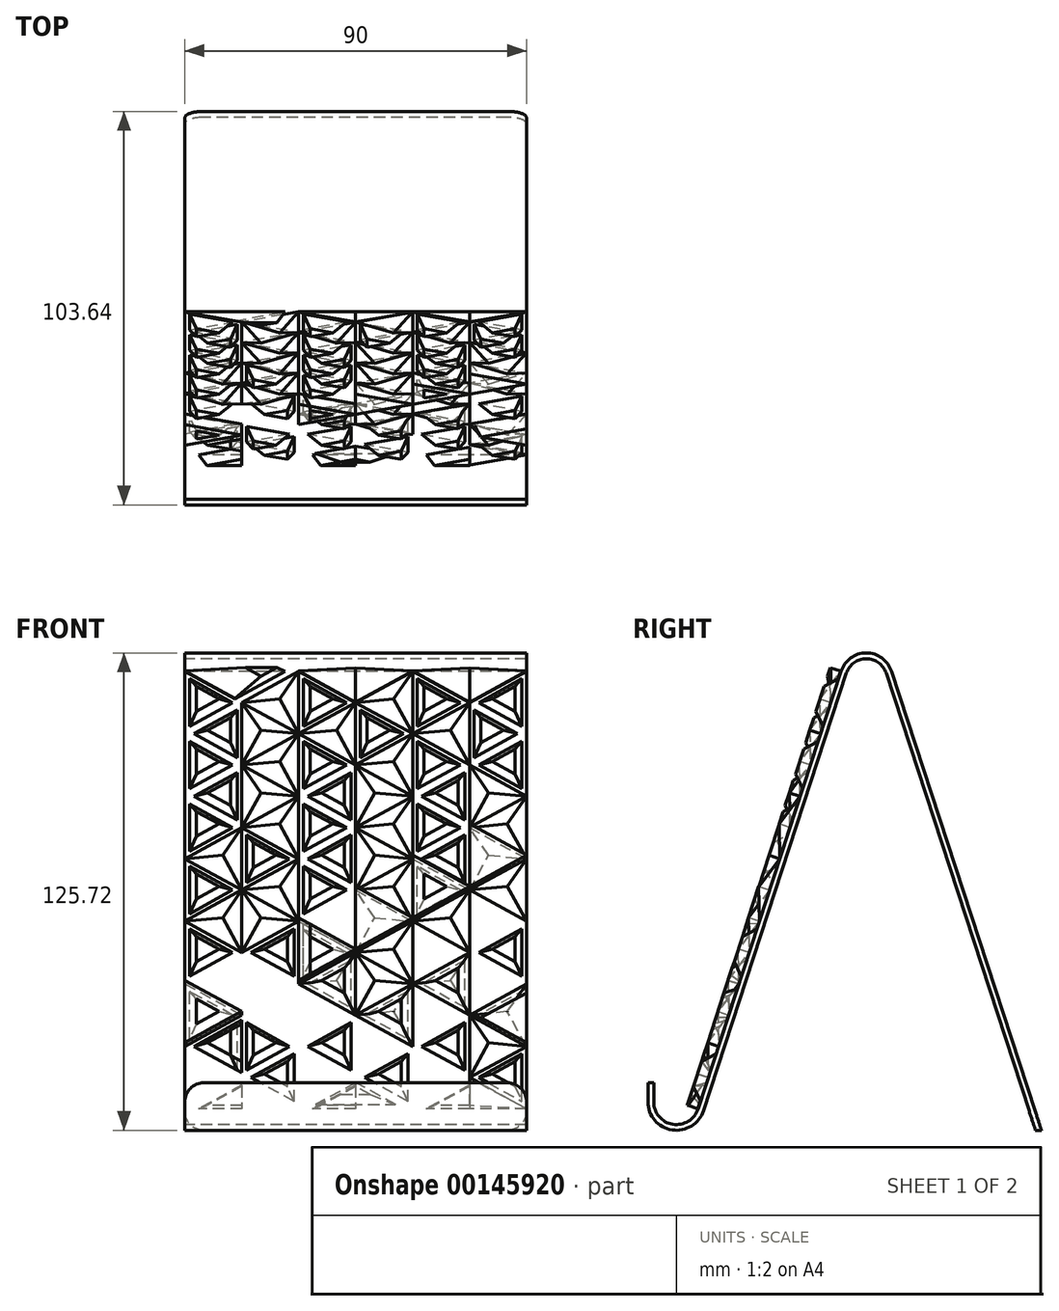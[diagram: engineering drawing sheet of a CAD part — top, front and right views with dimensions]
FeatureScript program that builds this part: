
annotation { "Feature Type Name" : "Feature", "Feature Type Description" : "" }
export const myFeature = defineFeature(function(context is Context, id is Id, definition is map)
    precondition{}
    {
        {
            var Q0;
            Q0=qCreatedBy(makeId("Right.planeOp"),FACE);
            var sketch = newSketch(context, id + "F0", { "sketchPlane" : qUnion([Q0])});
            skArc(sketch, "E0", {"start": v(-7.5, 0) * mm, "mid": v(-1.18, -7.4) * mm, "end": v(7.13, -2.33) * mm});
            skArc(sketch, "E1", {"start": v(55.23, 112.93) * mm, "mid": v(50, 116.72) * mm, "end": v(44.77, 112.93) * mm});
            skLineSegment(sketch, "E2", {"start": v(44.77, 112.93) * mm, "end": v(7.13, -2.33) * mm});
            skLineSegment(sketch, "E3", {"start": v(50, 111.22) * mm, "end": v(50, 0) * mm, "construction": true});
            skLineSegment(sketch, "E4.MirrorCS", {"start": v(55.23, 112.93) * mm, "end": v(94.56, -7.5) * mm});
            skLineSegment(sketch, "E5", {"start": v(0, -7.5) * mm, "end": v(108.37, -7.5) * mm, "construction": true});
            skLineSegment(sketch, "E6", {"start": v(-7.5, 0) * mm, "end": v(-7.5, 5) * mm});
            skLineSegment(sketch, "E7.0", {"start": v(-6, 0) * mm, "end": v(-6, 5) * mm});
            skLineSegment(sketch, "E7.1", {"start": v(56.65, 113.4) * mm, "end": v(96.14, -7.5) * mm});
            skArc(sketch, "E7.2", {"start": v(56.65, 113.4) * mm, "mid": v(50, 118.22) * mm, "end": v(43.35, 113.4) * mm});
            skLineSegment(sketch, "E7.3", {"start": v(43.35, 113.4) * mm, "end": v(5.7, -1.86) * mm});
            skArc(sketch, "E7.4", {"start": v(-6, 0) * mm, "mid": v(-0.94, -5.93) * mm, "end": v(5.7, -1.86) * mm});
            skLineSegment(sketch, "E8", {"start": v(94.56, -7.5) * mm, "end": v(96.14, -7.5) * mm});
            skLineSegment(sketch, "E9", {"start": v(-7.5, 5) * mm, "end": v(-6, 5) * mm});
            skSolve(sketch);
        }
        {
            var Q0;
            Q0=makeQuery(id+"F0.imprint","IMPRINT",FACE,{"disambiguationData":[TD([[makeQuery(id+"F0.imprint","IMPRINT",EDGE,{"derivedFrom":sQuery(id+"F0.wireOp",EDGE,"E0")}),1.0]])]});
            extrude(context, id + "F1", {"entities" : qUnion([Q0]), "depth" : 90 * mm, "symmetric" : true});
        }
        {
            var Q0;
            Q0=makeQuery(id+"F1.opExtrude","CAP_EDGE",EDGE,{"disambiguationData":[OSD([sQuery(id+"F0.wireOp",EDGE,"E9")])],"isStart":false});
            var Q1;
            Q1=makeQuery(id+"F1.opExtrude","CAP_EDGE",EDGE,{"disambiguationData":[OSD([sQuery(id+"F0.wireOp",EDGE,"E9")])],"isStart":true});
            var Q2;
            Q2=makeQuery(id+"F1.opExtrude","CAP_EDGE",EDGE,{"disambiguationData":[OSD([sQuery(id+"F0.wireOp",EDGE,"E8")])],"isStart":true});
            var Q3;
            Q3=makeQuery(id+"F1.opExtrude","CAP_EDGE",EDGE,{"disambiguationData":[OSD([sQuery(id+"F0.wireOp",EDGE,"E8")])],"isStart":false});
            fillet(context, id + "F2", {"entities" : qUnion([Q0, Q1, Q2, Q3]), "radius" : 5 * mm, "tangentPropagation" : true, "allowEdgeOverflow" : false});
        }
        {
            var Q0;
            Q0=makeQuery(id+"F1.opExtrude","SWEPT_FACE",FACE,{"disambiguationData":[OSD([sQuery(id+"F0.wireOp",EDGE,"E7.3")])]});
            var sketch = newSketch(context, id + "F3", { "sketchPlane" : qUnion([Q0])});
            skLineSegment(sketch, "E10", {"start": v(-45, 121.25) * mm, "end": v(45, 121.25) * mm});
            skLineSegment(sketch, "E11", {"start": v(45, 121.25) * mm, "end": v(45, 0) * mm});
            skLineSegment(sketch, "E12", {"start": v(45, 0) * mm, "end": v(-45, 0) * mm});
            skLineSegment(sketch, "E13", {"start": v(-45, 0) * mm, "end": v(-45, 121.25) * mm});
            skPoint(sketch, "E14", {"position": v(-45, 121.25) * mm});
            skPoint(sketch, "E15", {"position": v(45, 121.25) * mm});
            skPoint(sketch, "E16", {"position": v(45, 0) * mm});
            skPoint(sketch, "E17", {"position": v(-45, 0) * mm});
            skPoint(sketch, "E18", {"position": v(-15, 121.25) * mm});
            skPoint(sketch, "E19", {"position": v(15, 121.25) * mm});
            skLineSegment(sketch, "E20", {"start": v(-15, 121.25) * mm, "end": v(-15, 0) * mm});
            skLineSegment(sketch, "E21", {"start": v(15, 121.25) * mm, "end": v(15, 0) * mm});
            skPoint(sketch, "E22", {"position": v(-45, 103.93) * mm});
            skPoint(sketch, "E23", {"position": v(-45, 86.6) * mm});
            skPoint(sketch, "E24", {"position": v(-45, 69.28) * mm});
            skPoint(sketch, "E25", {"position": v(-45, 51.96) * mm});
            skPoint(sketch, "E26", {"position": v(-45, 34.64) * mm});
            skPoint(sketch, "E27", {"position": v(-45, 17.32) * mm});
            skLineSegment(sketch, "E28", {"start": v(-15, 103.93) * mm, "end": v(15, 121.25) * mm});
            skLineSegment(sketch, "E29", {"start": v(-15, 121.25) * mm, "end": v(-45, 103.93) * mm});
            skLineSegment(sketch, "E30", {"start": v(-45, 121.25) * mm, "end": v(45, 69.28) * mm});
            skLineSegment(sketch, "E31", {"start": v(-15, 103.93) * mm, "end": v(-45, 86.6) * mm});
            skLineSegment(sketch, "E32", {"start": v(-45, 103.93) * mm, "end": v(45, 51.96) * mm});
            skLineSegment(sketch, "E33", {"start": v(-45, 69.28) * mm, "end": v(45, 121.25) * mm});
            skLineSegment(sketch, "E34", {"start": v(-45, 51.96) * mm, "end": v(45, 103.93) * mm});
            skLineSegment(sketch, "E35", {"start": v(-15, 121.25) * mm, "end": v(45, 86.6) * mm});
            skLineSegment(sketch, "E36", {"start": v(15, 121.25) * mm, "end": v(45, 103.93) * mm});
            skLineSegment(sketch, "E37", {"start": v(-45, 86.6) * mm, "end": v(45, 34.64) * mm});
            skLineSegment(sketch, "E38", {"start": v(-45, 69.28) * mm, "end": v(-15, 51.96) * mm});
            skLineSegment(sketch, "E39", {"start": v(45, 86.6) * mm, "end": v(-15, 51.96) * mm});
            skLineSegment(sketch, "E40", {"start": v(45, 69.28) * mm, "end": v(-45, 17.32) * mm});
            skLineSegment(sketch, "E41", {"start": v(-45, 0) * mm, "end": v(45, 51.96) * mm});
            skLineSegment(sketch, "E42", {"start": v(-45, 34.64) * mm, "end": v(-15, 51.96) * mm});
            skLineSegment(sketch, "E43", {"start": v(-45, 51.96) * mm, "end": v(-15, 34.64) * mm});
            skLineSegment(sketch, "E44", {"start": v(-45, 34.64) * mm, "end": v(15, 0) * mm});
            skLineSegment(sketch, "E45", {"start": v(15, 17.32) * mm, "end": v(15, 17.32) * mm});
            skLineSegment(sketch, "E46", {"start": v(-45, 17.32) * mm, "end": v(-15, 0) * mm});
            skLineSegment(sketch, "E47", {"start": v(-15, 51.96) * mm, "end": v(45, 17.32) * mm});
            skLineSegment(sketch, "E48", {"start": v(-15, 0) * mm, "end": v(15, 17.32) * mm});
            skLineSegment(sketch, "E49", {"start": v(-15, 34.64) * mm, "end": v(-15, 34.64) * mm});
            skLineSegment(sketch, "E50", {"start": v(45, 0) * mm, "end": v(-15, 34.64) * mm});
            skLineSegment(sketch, "E51", {"start": v(15, 17.32) * mm, "end": v(45, 34.64) * mm});
            skLineSegment(sketch, "E52", {"start": v(15, 0) * mm, "end": v(45, 17.32) * mm});
            skPoint(sketch, "E53", {"position": v(0, 112.59) * mm});
            skLineSegment(sketch, "E54", {"start": v(0, 121.25) * mm, "end": v(0, 0) * mm});
            skPoint(sketch, "E55", {"position": v(-30, 112.59) * mm});
            skLineSegment(sketch, "E56", {"start": v(-30, 121.25) * mm, "end": v(-30, 0) * mm});
            skPoint(sketch, "E56.endSnap0", {"position": v(-30, 8.66) * mm});
            skPoint(sketch, "E57", {"position": v(30, 112.59) * mm});
            skLineSegment(sketch, "E58", {"start": v(30, 121.25) * mm, "end": v(30, 0) * mm});
            skPoint(sketch, "E58.endSnap0", {"position": v(30, 25.98) * mm});
            skPoint(sketch, "E59", {"position": v(-30, 95.27) * mm});
            skPoint(sketch, "E60", {"position": v(-30, 77.94) * mm});
            skPoint(sketch, "E61", {"position": v(-30, 60.62) * mm});
            skPoint(sketch, "E62", {"position": v(-30, 43.3) * mm});
            skPoint(sketch, "E63", {"position": v(-30, 25.98) * mm});
            skPoint(sketch, "E64", {"position": v(-30, 0) * mm});
            skPoint(sketch, "E65", {"position": v(-15, 17.32) * mm});
            skPoint(sketch, "E66", {"position": v(-15, 34.64) * mm});
            skPoint(sketch, "E67", {"position": v(-15, 51.96) * mm});
            skPoint(sketch, "E68", {"position": v(-15, 69.28) * mm});
            skPoint(sketch, "E69", {"position": v(-15, 86.6) * mm});
            skPoint(sketch, "E70", {"position": v(0, 8.66) * mm});
            skPoint(sketch, "E71", {"position": v(0, 25.98) * mm});
            skPoint(sketch, "E72", {"position": v(0, 43.3) * mm});
            skPoint(sketch, "E73", {"position": v(0, 60.62) * mm});
            skPoint(sketch, "E74", {"position": v(15, 103.93) * mm});
            skPoint(sketch, "E75", {"position": v(0, 95.27) * mm});
            skPoint(sketch, "E76", {"position": v(0, 77.94) * mm});
            skPoint(sketch, "E77", {"position": v(15, 69.28) * mm});
            skPoint(sketch, "E78", {"position": v(15, 86.6) * mm});
            skPoint(sketch, "E79", {"position": v(15, 51.96) * mm});
            skPoint(sketch, "E80", {"position": v(15, 34.64) * mm});
            skPoint(sketch, "E81", {"position": v(15, 17.32) * mm});
            skPoint(sketch, "E82", {"position": v(15, 0) * mm});
            skPoint(sketch, "E83", {"position": v(30, 8.66) * mm});
            skPoint(sketch, "E84", {"position": v(30, 43.3) * mm});
            skPoint(sketch, "E85", {"position": v(30, 60.62) * mm});
            skPoint(sketch, "E86", {"position": v(30, 77.94) * mm});
            skPoint(sketch, "E87", {"position": v(30, 95.27) * mm});
            skPoint(sketch, "E88", {"position": v(45, 103.93) * mm});
            skSolve(sketch);
        }
        {
            var Q0;
            {var subQ0=sQuery(id+"F3.wireOp",EDGE,"E30");var subQ1=sQuery(id+"F3.wireOp",EDGE,"E13");var subQ2=makeQuery(id+"F3.imprint","INTERSECT",VERTEX,{"derivedFrom":[sQuery(id+"F3.wireOp",EDGE,"E10"),subQ1,subQ0]});Q0=makeQuery(id+"F3.imprint","IMPRINT",FACE,{"disambiguationData":[TD([[makeQuery(id+"F3.imprint","IMPRINT",EDGE,{"disambiguationData":[TD([[subQ2,-1.0]])],"derivedFrom":subQ1}),1.0]])]});}
            var Q1;
            {var subQ0=sQuery(id+"F3.wireOp",EDGE,"E29");var subQ3=sQuery(id+"F3.wireOp",EDGE,"E30");var subQ5=makeQuery(id+"F3.imprint","INTERSECT",VERTEX,{"derivedFrom":[subQ0,subQ3,sQuery(id+"F3.wireOp",EDGE,"E56")]});Q1=makeQuery(id+"F3.imprint","IMPRINT",FACE,{"disambiguationData":[TD([[makeQuery(id+"F3.imprint","IMPRINT",EDGE,{"disambiguationData":[TD([[subQ5,1.0]])],"derivedFrom":subQ0}),1.0]])]});}
            var Q2;
            {var subQ0=sQuery(id+"F3.wireOp",EDGE,"E32");var subQ1=sQuery(id+"F3.wireOp",EDGE,"E13");var subQ2=makeQuery(id+"F3.imprint","INTERSECT",VERTEX,{"derivedFrom":[subQ1,sQuery(id+"F3.wireOp",EDGE,"E29"),subQ0]});Q2=makeQuery(id+"F3.imprint","IMPRINT",FACE,{"disambiguationData":[TD([[makeQuery(id+"F3.imprint","IMPRINT",EDGE,{"disambiguationData":[TD([[subQ2,-1.0]])],"derivedFrom":subQ1}),1.0]])]});}
            var Q3;
            {var subQ1=sQuery(id+"F3.wireOp",EDGE,"E20");var subQ3=sQuery(id+"F3.wireOp",EDGE,"E32");var subQ4=makeQuery(id+"F3.imprint","INTERSECT",VERTEX,{"derivedFrom":[subQ1,subQ3,sQuery(id+"F3.wireOp",EDGE,"E33")]});Q3=makeQuery(id+"F3.imprint","IMPRINT",FACE,{"disambiguationData":[TD([[makeQuery(id+"F3.imprint","IMPRINT",EDGE,{"disambiguationData":[TD([[subQ4,1.0]])],"derivedFrom":subQ3}),1.0]])]});}
            var Q4;
            {var subQ0=sQuery(id+"F3.wireOp",EDGE,"E37");var subQ1=sQuery(id+"F3.wireOp",EDGE,"E13");var subQ2=makeQuery(id+"F3.imprint","INTERSECT",VERTEX,{"derivedFrom":[subQ1,sQuery(id+"F3.wireOp",EDGE,"E31"),subQ0]});Q4=makeQuery(id+"F3.imprint","IMPRINT",FACE,{"disambiguationData":[TD([[makeQuery(id+"F3.imprint","IMPRINT",EDGE,{"disambiguationData":[TD([[subQ2,-1.0]])],"derivedFrom":subQ1}),1.0]])]});}
            var Q5;
            {var subQ0=sQuery(id+"F3.wireOp",EDGE,"E33");var subQ1=sQuery(id+"F3.wireOp",EDGE,"E20");var subQ2=makeQuery(id+"F3.imprint","INTERSECT",VERTEX,{"derivedFrom":[subQ1,sQuery(id+"F3.wireOp",EDGE,"E32"),subQ0]});Q5=makeQuery(id+"F3.imprint","IMPRINT",FACE,{"disambiguationData":[TD([[makeQuery(id+"F3.imprint","IMPRINT",EDGE,{"disambiguationData":[TD([[subQ2,-1.0]])],"derivedFrom":subQ1}),-1.0]])]});}
            var Q6;
            {var subQ0=sQuery(id+"F3.wireOp",EDGE,"E38");var subQ1=sQuery(id+"F3.wireOp",EDGE,"E13");var subQ2=makeQuery(id+"F3.imprint","INTERSECT",VERTEX,{"derivedFrom":[subQ1,sQuery(id+"F3.wireOp",EDGE,"E33"),subQ0]});Q6=makeQuery(id+"F3.imprint","IMPRINT",FACE,{"disambiguationData":[TD([[makeQuery(id+"F3.imprint","IMPRINT",EDGE,{"disambiguationData":[TD([[subQ2,-1.0]])],"derivedFrom":subQ1}),1.0]])]});}
            var Q7;
            {var subQ1=sQuery(id+"F3.wireOp",EDGE,"E20");var subQ3=sQuery(id+"F3.wireOp",EDGE,"E34");var subQ4=makeQuery(id+"F3.imprint","INTERSECT",VERTEX,{"derivedFrom":[subQ1,subQ3,sQuery(id+"F3.wireOp",EDGE,"E37")]});Q7=makeQuery(id+"F3.imprint","IMPRINT",FACE,{"disambiguationData":[TD([[makeQuery(id+"F3.imprint","IMPRINT",EDGE,{"disambiguationData":[TD([[subQ4,1.0]])],"derivedFrom":subQ3}),-1.0]])]});}
            var Q8;
            {var subQ0=sQuery(id+"F3.wireOp",EDGE,"E43");var subQ1=sQuery(id+"F3.wireOp",EDGE,"E13");var subQ2=makeQuery(id+"F3.imprint","INTERSECT",VERTEX,{"derivedFrom":[subQ1,sQuery(id+"F3.wireOp",EDGE,"E34"),subQ0]});Q8=makeQuery(id+"F3.imprint","IMPRINT",FACE,{"disambiguationData":[TD([[makeQuery(id+"F3.imprint","IMPRINT",EDGE,{"disambiguationData":[TD([[subQ2,-1.0]])],"derivedFrom":subQ1}),1.0]])]});}
            var Q9;
            {var subQ0=sQuery(id+"F3.wireOp",EDGE,"E42");var subQ3=sQuery(id+"F3.wireOp",EDGE,"E43");var subQ5=makeQuery(id+"F3.imprint","INTERSECT",VERTEX,{"derivedFrom":[subQ0,subQ3,sQuery(id+"F3.wireOp",EDGE,"E56")]});Q9=makeQuery(id+"F3.imprint","IMPRINT",FACE,{"disambiguationData":[TD([[makeQuery(id+"F3.imprint","IMPRINT",EDGE,{"disambiguationData":[TD([[subQ5,-1.0]])],"derivedFrom":subQ3}),1.0]])]});}
            var Q10;
            {var subQ0=sQuery(id+"F3.wireOp",EDGE,"E40");var subQ3=sQuery(id+"F3.wireOp",EDGE,"E44");var subQ5=makeQuery(id+"F3.imprint","INTERSECT",VERTEX,{"derivedFrom":[subQ0,subQ3]});Q10=makeQuery(id+"F3.imprint","IMPRINT",FACE,{"disambiguationData":[TD([[makeQuery(id+"F3.imprint","IMPRINT",EDGE,{"disambiguationData":[TD([[subQ5,-1.0]])],"derivedFrom":subQ0}),-1.0]])]});}
            var Q11;
            {var subQ0=sQuery(id+"F3.wireOp",EDGE,"E49");var subQ1=sQuery(id+"F3.wireOp",EDGE,"E40");var subQ2=makeQuery(id+"F3.imprint","INTERSECT",VERTEX,{"derivedFrom":[subQ1,subQ0]});Q11=makeQuery(id+"F3.imprint","IMPRINT",FACE,{"disambiguationData":[TD([[makeQuery(id+"F3.imprint","IMPRINT",EDGE,{"disambiguationData":[TD([[subQ2,-1.0]])],"derivedFrom":subQ1}),1.0]])]});}
            var Q12;
            {var subQ0=sQuery(id+"F3.wireOp",EDGE,"E41");var subQ5=sQuery(id+"F3.wireOp",EDGE,"E56");var subQ6=makeQuery(id+"F3.imprint","INTERSECT",VERTEX,{"derivedFrom":[subQ0,subQ5]});Q12=makeQuery(id+"F3.imprint","IMPRINT",FACE,{"disambiguationData":[TD([[makeQuery(id+"F3.imprint","IMPRINT",EDGE,{"disambiguationData":[TD([[subQ6,1.0]])],"derivedFrom":subQ5}),-1.0]])]});}
            var Q13;
            {var subQ0=sQuery(id+"F3.wireOp",EDGE,"E46");var subQ3=sQuery(id+"F3.wireOp",EDGE,"E41");var subQ5=makeQuery(id+"F3.imprint","INTERSECT",VERTEX,{"derivedFrom":[subQ3,subQ0]});Q13=makeQuery(id+"F3.imprint","IMPRINT",FACE,{"disambiguationData":[TD([[makeQuery(id+"F3.imprint","IMPRINT",EDGE,{"disambiguationData":[TD([[subQ5,-1.0]])],"derivedFrom":subQ3}),-1.0]])]});}
            var Q14;
            {var subQ1=sQuery(id+"F3.wireOp",EDGE,"E10");var subQ3=sQuery(id+"F3.wireOp",EDGE,"E54");var subQ4=makeQuery(id+"F3.imprint","INTERSECT",VERTEX,{"derivedFrom":[subQ1,subQ3]});Q14=makeQuery(id+"F3.imprint","IMPRINT",FACE,{"disambiguationData":[TD([[makeQuery(id+"F3.imprint","IMPRINT",EDGE,{"disambiguationData":[TD([[subQ4,-1.0]])],"derivedFrom":subQ3}),-1.0]])]});}
            var Q15;
            {var subQ1=sQuery(id+"F3.wireOp",EDGE,"E28");var subQ3=sQuery(id+"F3.wireOp",EDGE,"E54");var subQ4=makeQuery(id+"F3.imprint","INTERSECT",VERTEX,{"derivedFrom":[subQ1,sQuery(id+"F3.wireOp",EDGE,"E35"),subQ3]});Q15=makeQuery(id+"F3.imprint","IMPRINT",FACE,{"disambiguationData":[TD([[makeQuery(id+"F3.imprint","IMPRINT",EDGE,{"disambiguationData":[TD([[subQ4,-1.0]])],"derivedFrom":subQ3}),-1.0]])]});}
            var Q16;
            {var subQ0=sQuery(id+"F3.wireOp",EDGE,"E33");var subQ1=sQuery(id+"F3.wireOp",EDGE,"E32");var subQ2=makeQuery(id+"F3.imprint","INTERSECT",VERTEX,{"derivedFrom":[sQuery(id+"F3.wireOp",EDGE,"E20"),subQ1,subQ0]});Q16=makeQuery(id+"F3.imprint","IMPRINT",FACE,{"disambiguationData":[TD([[makeQuery(id+"F3.imprint","IMPRINT",EDGE,{"disambiguationData":[TD([[subQ2,-1.0]])],"derivedFrom":subQ1}),1.0]])]});}
            var Q17;
            {var subQ0=sQuery(id+"F3.wireOp",EDGE,"E37");var subQ1=sQuery(id+"F3.wireOp",EDGE,"E34");var subQ2=makeQuery(id+"F3.imprint","INTERSECT",VERTEX,{"derivedFrom":[sQuery(id+"F3.wireOp",EDGE,"E20"),subQ1,subQ0]});Q17=makeQuery(id+"F3.imprint","IMPRINT",FACE,{"disambiguationData":[TD([[makeQuery(id+"F3.imprint","IMPRINT",EDGE,{"disambiguationData":[TD([[subQ2,-1.0]])],"derivedFrom":subQ1}),-1.0]])]});}
            var Q18;
            {var subQ3=sQuery(id+"F3.wireOp",EDGE,"E54");var subQ5=sQuery(id+"F3.wireOp",EDGE,"E40");var subQ6=makeQuery(id+"F3.imprint","INTERSECT",VERTEX,{"derivedFrom":[subQ5,subQ3]});Q18=makeQuery(id+"F3.imprint","IMPRINT",FACE,{"disambiguationData":[TD([[makeQuery(id+"F3.imprint","IMPRINT",EDGE,{"disambiguationData":[TD([[subQ6,-1.0]])],"derivedFrom":subQ5}),-1.0]])]});}
            var Q19;
            {var subQ1=sQuery(id+"F3.wireOp",EDGE,"E40");var subQ6=sQuery(id+"F3.wireOp",EDGE,"E47");var subQ7=makeQuery(id+"F3.imprint","INTERSECT",VERTEX,{"derivedFrom":[subQ1,subQ6]});Q19=makeQuery(id+"F3.imprint","IMPRINT",FACE,{"disambiguationData":[TD([[makeQuery(id+"F3.imprint","IMPRINT",EDGE,{"disambiguationData":[TD([[subQ7,-1.0]])],"derivedFrom":subQ6}),-1.0]])]});}
            var Q20;
            {var subQ0=sQuery(id+"F3.wireOp",EDGE,"E54");var subQ1=sQuery(id+"F3.wireOp",EDGE,"E41");var subQ2=makeQuery(id+"F3.imprint","INTERSECT",VERTEX,{"derivedFrom":[subQ1,subQ0]});Q20=makeQuery(id+"F3.imprint","IMPRINT",FACE,{"disambiguationData":[TD([[makeQuery(id+"F3.imprint","IMPRINT",EDGE,{"disambiguationData":[TD([[subQ2,-1.0]])],"derivedFrom":subQ0}),-1.0]])]});}
            var Q21;
            {var subQ1=sQuery(id+"F3.wireOp",EDGE,"E12");var subQ3=sQuery(id+"F3.wireOp",EDGE,"E54");var subQ4=makeQuery(id+"F3.imprint","INTERSECT",VERTEX,{"derivedFrom":[subQ1,subQ3]});Q21=makeQuery(id+"F3.imprint","IMPRINT",FACE,{"disambiguationData":[TD([[makeQuery(id+"F3.imprint","IMPRINT",EDGE,{"disambiguationData":[TD([[subQ4,1.0]])],"derivedFrom":subQ3}),-1.0]])]});}
            var Q22;
            {var subQ1=sQuery(id+"F3.wireOp",EDGE,"E12");var subQ3=sQuery(id+"F3.wireOp",EDGE,"E44");var subQ4=makeQuery(id+"F3.imprint","INTERSECT",VERTEX,{"derivedFrom":[subQ1,subQ3]});Q22=makeQuery(id+"F3.imprint","IMPRINT",FACE,{"disambiguationData":[TD([[makeQuery(id+"F3.imprint","IMPRINT",EDGE,{"disambiguationData":[TD([[subQ4,1.0]])],"derivedFrom":subQ3}),1.0]])]});}
            var Q23;
            {var subQ0=sQuery(id+"F3.wireOp",EDGE,"E50");var subQ1=sQuery(id+"F3.wireOp",EDGE,"E21");var subQ2=makeQuery(id+"F3.imprint","INTERSECT",VERTEX,{"derivedFrom":[subQ1,subQ0]});Q23=makeQuery(id+"F3.imprint","IMPRINT",FACE,{"disambiguationData":[TD([[makeQuery(id+"F3.imprint","IMPRINT",EDGE,{"disambiguationData":[TD([[subQ2,-1.0]])],"derivedFrom":subQ0}),-1.0]])]});}
            var Q24;
            {var subQ0=sQuery(id+"F3.wireOp",EDGE,"E40");var subQ5=sQuery(id+"F3.wireOp",EDGE,"E54");var subQ7=makeQuery(id+"F3.imprint","INTERSECT",VERTEX,{"derivedFrom":[subQ0,subQ5]});Q24=makeQuery(id+"F3.imprint","IMPRINT",FACE,{"disambiguationData":[TD([[makeQuery(id+"F3.imprint","IMPRINT",EDGE,{"disambiguationData":[TD([[subQ7,-1.0]])],"derivedFrom":subQ5}),1.0]])]});}
            var Q25;
            {var subQ0=sQuery(id+"F3.wireOp",EDGE,"E39");var subQ1=sQuery(id+"F3.wireOp",EDGE,"E21");var subQ2=makeQuery(id+"F3.imprint","INTERSECT",VERTEX,{"derivedFrom":[subQ1,sQuery(id+"F3.wireOp",EDGE,"E32"),subQ0]});Q25=makeQuery(id+"F3.imprint","IMPRINT",FACE,{"disambiguationData":[TD([[makeQuery(id+"F3.imprint","IMPRINT",EDGE,{"disambiguationData":[TD([[subQ2,-1.0]])],"derivedFrom":subQ1}),-1.0]])]});}
            var Q26;
            {var subQ0=sQuery(id+"F3.wireOp",EDGE,"E34");var subQ1=sQuery(id+"F3.wireOp",EDGE,"E21");var subQ2=makeQuery(id+"F3.imprint","INTERSECT",VERTEX,{"derivedFrom":[subQ1,sQuery(id+"F3.wireOp",EDGE,"E30"),subQ0]});Q26=makeQuery(id+"F3.imprint","IMPRINT",FACE,{"disambiguationData":[TD([[makeQuery(id+"F3.imprint","IMPRINT",EDGE,{"disambiguationData":[TD([[subQ2,-1.0]])],"derivedFrom":subQ1}),-1.0]])]});}
            var Q27;
            {var subQ0=sQuery(id+"F3.wireOp",EDGE,"E33");var subQ1=sQuery(id+"F3.wireOp",EDGE,"E21");var subQ2=makeQuery(id+"F3.imprint","INTERSECT",VERTEX,{"derivedFrom":[subQ1,subQ0,sQuery(id+"F3.wireOp",EDGE,"E35")]});Q27=makeQuery(id+"F3.imprint","IMPRINT",FACE,{"disambiguationData":[TD([[makeQuery(id+"F3.imprint","IMPRINT",EDGE,{"disambiguationData":[TD([[subQ2,-1.0]])],"derivedFrom":subQ1}),-1.0]])]});}
            var Q28;
            {var subQ1=sQuery(id+"F3.wireOp",EDGE,"E21");var subQ3=sQuery(id+"F3.wireOp",EDGE,"E35");var subQ4=makeQuery(id+"F3.imprint","INTERSECT",VERTEX,{"derivedFrom":[subQ1,sQuery(id+"F3.wireOp",EDGE,"E33"),subQ3]});Q28=makeQuery(id+"F3.imprint","IMPRINT",FACE,{"disambiguationData":[TD([[makeQuery(id+"F3.imprint","IMPRINT",EDGE,{"disambiguationData":[TD([[subQ4,1.0]])],"derivedFrom":subQ3}),1.0]])]});}
            var Q29;
            {var subQ1=sQuery(id+"F3.wireOp",EDGE,"E10");var subQ3=sQuery(id+"F3.wireOp",EDGE,"E58");var subQ4=makeQuery(id+"F3.imprint","INTERSECT",VERTEX,{"derivedFrom":[subQ1,subQ3]});Q29=makeQuery(id+"F3.imprint","IMPRINT",FACE,{"disambiguationData":[TD([[makeQuery(id+"F3.imprint","IMPRINT",EDGE,{"disambiguationData":[TD([[subQ4,-1.0]])],"derivedFrom":subQ3}),-1.0]])]});}
            var Q30;
            {var subQ0=sQuery(id+"F3.wireOp",EDGE,"E35");var subQ1=sQuery(id+"F3.wireOp",EDGE,"E33");var subQ2=makeQuery(id+"F3.imprint","INTERSECT",VERTEX,{"derivedFrom":[sQuery(id+"F3.wireOp",EDGE,"E21"),subQ1,subQ0]});Q30=makeQuery(id+"F3.imprint","IMPRINT",FACE,{"disambiguationData":[TD([[makeQuery(id+"F3.imprint","IMPRINT",EDGE,{"disambiguationData":[TD([[subQ2,-1.0]])],"derivedFrom":subQ1}),-1.0]])]});}
            var Q31;
            {var subQ0=sQuery(id+"F3.wireOp",EDGE,"E34");var subQ1=sQuery(id+"F3.wireOp",EDGE,"E30");var subQ2=makeQuery(id+"F3.imprint","INTERSECT",VERTEX,{"derivedFrom":[sQuery(id+"F3.wireOp",EDGE,"E21"),subQ1,subQ0]});Q31=makeQuery(id+"F3.imprint","IMPRINT",FACE,{"disambiguationData":[TD([[makeQuery(id+"F3.imprint","IMPRINT",EDGE,{"disambiguationData":[TD([[subQ2,-1.0]])],"derivedFrom":subQ1}),1.0]])]});}
            var Q32;
            {var subQ0=sQuery(id+"F3.wireOp",EDGE,"E39");var subQ1=sQuery(id+"F3.wireOp",EDGE,"E32");var subQ2=makeQuery(id+"F3.imprint","INTERSECT",VERTEX,{"derivedFrom":[sQuery(id+"F3.wireOp",EDGE,"E21"),subQ1,subQ0]});Q32=makeQuery(id+"F3.imprint","IMPRINT",FACE,{"disambiguationData":[TD([[makeQuery(id+"F3.imprint","IMPRINT",EDGE,{"disambiguationData":[TD([[subQ2,-1.0]])],"derivedFrom":subQ1}),1.0]])]});}
            var Q33;
            {var subQ0=sQuery(id+"F3.wireOp",EDGE,"E58");var subQ1=sQuery(id+"F3.wireOp",EDGE,"E37");var subQ2=makeQuery(id+"F3.imprint","INTERSECT",VERTEX,{"derivedFrom":[subQ1,subQ0]});Q33=makeQuery(id+"F3.imprint","IMPRINT",FACE,{"disambiguationData":[TD([[makeQuery(id+"F3.imprint","IMPRINT",EDGE,{"disambiguationData":[TD([[subQ2,1.0]])],"derivedFrom":subQ1}),1.0]])]});}
            var Q34;
            {var subQ0=sQuery(id+"F3.wireOp",EDGE,"E58");var subQ1=sQuery(id+"F3.wireOp",EDGE,"E41");var subQ2=makeQuery(id+"F3.imprint","INTERSECT",VERTEX,{"derivedFrom":[subQ1,subQ0]});Q34=makeQuery(id+"F3.imprint","IMPRINT",FACE,{"disambiguationData":[TD([[makeQuery(id+"F3.imprint","IMPRINT",EDGE,{"disambiguationData":[TD([[subQ2,-1.0]])],"derivedFrom":subQ0}),-1.0]])]});}
            var Q35;
            {var subQ0=sQuery(id+"F3.wireOp",EDGE,"E50");var subQ1=makeQuery(id+"F3.imprint","INTERSECT",VERTEX,{"derivedFrom":[sQuery(id+"F3.wireOp",EDGE,"E45"),subQ0]});Q35=makeQuery(id+"F3.imprint","IMPRINT",FACE,{"disambiguationData":[TD([[makeQuery(id+"F3.imprint","IMPRINT",EDGE,{"disambiguationData":[TD([[subQ1,1.0]])],"derivedFrom":subQ0}),-1.0]])]});}
            var Q36;
            {var subQ1=sQuery(id+"F3.wireOp",EDGE,"E12");var subQ3=sQuery(id+"F3.wireOp",EDGE,"E58");var subQ4=makeQuery(id+"F3.imprint","INTERSECT",VERTEX,{"derivedFrom":[subQ1,subQ3]});Q36=makeQuery(id+"F3.imprint","IMPRINT",FACE,{"disambiguationData":[TD([[makeQuery(id+"F3.imprint","IMPRINT",EDGE,{"disambiguationData":[TD([[subQ4,1.0]])],"derivedFrom":subQ3}),-1.0]])]});}
            var Q37;
            {var subQ0=sQuery(id+"F3.wireOp",EDGE,"E33");var subQ1=sQuery(id+"F3.wireOp",EDGE,"E11");var subQ2=makeQuery(id+"F3.imprint","INTERSECT",VERTEX,{"derivedFrom":[sQuery(id+"F3.wireOp",EDGE,"E10"),subQ1,subQ0]});Q37=makeQuery(id+"F3.imprint","IMPRINT",FACE,{"disambiguationData":[TD([[makeQuery(id+"F3.imprint","IMPRINT",EDGE,{"disambiguationData":[TD([[subQ2,-1.0]])],"derivedFrom":subQ1}),-1.0]])]});}
            var Q38;
            {var subQ0=sQuery(id+"F3.wireOp",EDGE,"E34");var subQ1=sQuery(id+"F3.wireOp",EDGE,"E11");var subQ2=makeQuery(id+"F3.imprint","INTERSECT",VERTEX,{"derivedFrom":[subQ1,subQ0,sQuery(id+"F3.wireOp",EDGE,"E36")]});Q38=makeQuery(id+"F3.imprint","IMPRINT",FACE,{"disambiguationData":[TD([[makeQuery(id+"F3.imprint","IMPRINT",EDGE,{"disambiguationData":[TD([[subQ2,-1.0]])],"derivedFrom":subQ1}),-1.0]])]});}
            var Q39;
            {var subQ0=sQuery(id+"F3.wireOp",EDGE,"E30");var subQ1=sQuery(id+"F3.wireOp",EDGE,"E11");var subQ2=makeQuery(id+"F3.imprint","INTERSECT",VERTEX,{"derivedFrom":[subQ1,subQ0,sQuery(id+"F3.wireOp",EDGE,"E40")]});Q39=makeQuery(id+"F3.imprint","IMPRINT",FACE,{"disambiguationData":[TD([[makeQuery(id+"F3.imprint","IMPRINT",EDGE,{"disambiguationData":[TD([[subQ2,1.0]])],"derivedFrom":subQ1}),-1.0]])]});}
            var Q40;
            {var subQ0=sQuery(id+"F3.wireOp",EDGE,"E40");var subQ1=sQuery(id+"F3.wireOp",EDGE,"E11");var subQ2=makeQuery(id+"F3.imprint","INTERSECT",VERTEX,{"derivedFrom":[subQ1,sQuery(id+"F3.wireOp",EDGE,"E30"),subQ0]});Q40=makeQuery(id+"F3.imprint","IMPRINT",FACE,{"disambiguationData":[TD([[makeQuery(id+"F3.imprint","IMPRINT",EDGE,{"disambiguationData":[TD([[subQ2,-1.0]])],"derivedFrom":subQ1}),-1.0]])]});}
            var Q41;
            {var subQ1=sQuery(id+"F3.wireOp",EDGE,"E11");var subQ3=sQuery(id+"F3.wireOp",EDGE,"E37");var subQ4=makeQuery(id+"F3.imprint","INTERSECT",VERTEX,{"derivedFrom":[subQ1,subQ3]});Q41=makeQuery(id+"F3.imprint","IMPRINT",FACE,{"disambiguationData":[TD([[makeQuery(id+"F3.imprint","IMPRINT",EDGE,{"disambiguationData":[TD([[subQ4,1.0]])],"derivedFrom":subQ3}),1.0]])]});}
            var Q42;
            {var subQ0=sQuery(id+"F3.wireOp",EDGE,"E51");var subQ1=sQuery(id+"F3.wireOp",EDGE,"E11");var subQ2=makeQuery(id+"F3.imprint","INTERSECT",VERTEX,{"derivedFrom":[subQ1,subQ0]});Q42=makeQuery(id+"F3.imprint","IMPRINT",FACE,{"disambiguationData":[TD([[makeQuery(id+"F3.imprint","IMPRINT",EDGE,{"disambiguationData":[TD([[subQ2,-1.0]])],"derivedFrom":subQ1}),-1.0]])]});}
            var Q43;
            {var subQ1=sQuery(id+"F3.wireOp",EDGE,"E11");var subQ3=sQuery(id+"F3.wireOp",EDGE,"E52");var subQ4=makeQuery(id+"F3.imprint","INTERSECT",VERTEX,{"derivedFrom":[subQ1,subQ3]});Q43=makeQuery(id+"F3.imprint","IMPRINT",FACE,{"disambiguationData":[TD([[makeQuery(id+"F3.imprint","IMPRINT",EDGE,{"disambiguationData":[TD([[subQ4,1.0]])],"derivedFrom":subQ3}),-1.0]])]});}
            extrude(context, id + "F4", {"entities" : qUnion([Q0, Q1, Q2, Q3, Q4, Q5, Q6, Q7, Q8, Q9, Q10, Q11, Q12, Q13, Q14, Q15, Q16, Q17, Q18, Q19, Q20, Q21, Q22, Q23, Q24, Q25, Q26, Q27, Q28, Q29, Q30, Q31, Q32, Q33, Q34, Q35, Q36, Q37, Q38, Q39, Q40, Q41, Q42, Q43]), "depth" : 3 * mm});
        }
        {
            var Q0;
            {var subQ0=sQuery(id+"F3.wireOp",EDGE,"E30");Q0=makeQuery(id+"F4.opExtrude","CAP_EDGE",EDGE,{"disambiguationData":[OSD([subQ0]),TDD([makeQuery(id+"F3.imprint","IMPRINT",EDGE,{"disambiguationData":[TD([[makeQuery(id+"F3.imprint","INTERSECT",VERTEX,{"derivedFrom":[sQuery(id+"F3.wireOp",EDGE,"E10"),sQuery(id+"F3.wireOp",EDGE,"E13"),subQ0]}),-1.0]])],"derivedFrom":subQ0})])],"isStart":false});}
            var Q1;
            {var subQ0=sQuery(id+"F3.wireOp",EDGE,"E13");Q1=makeQuery(id+"F4.opExtrude","CAP_EDGE",EDGE,{"disambiguationData":[OSD([subQ0]),TDD([makeQuery(id+"F3.imprint","IMPRINT",EDGE,{"disambiguationData":[TD([[makeQuery(id+"F3.imprint","INTERSECT",VERTEX,{"derivedFrom":[sQuery(id+"F3.wireOp",EDGE,"E10"),subQ0,sQuery(id+"F3.wireOp",EDGE,"E30")]}),-1.0]])],"derivedFrom":subQ0})])],"isStart":false});}
            var Q2;
            {var subQ0=sQuery(id+"F3.wireOp",EDGE,"E29");Q2=makeQuery(id+"F4.opExtrude","CAP_EDGE",EDGE,{"disambiguationData":[OSD([subQ0]),TDD([makeQuery(id+"F3.imprint","IMPRINT",EDGE,{"disambiguationData":[TD([[makeQuery(id+"F3.imprint","INTERSECT",VERTEX,{"derivedFrom":[sQuery(id+"F3.wireOp",EDGE,"E13"),subQ0,sQuery(id+"F3.wireOp",EDGE,"E32")]}),1.0]])],"derivedFrom":subQ0})])],"isStart":false});}
            var Q3;
            {var subQ0=sQuery(id+"F3.wireOp",EDGE,"E32");Q3=makeQuery(id+"F4.opExtrude","CAP_EDGE",EDGE,{"disambiguationData":[OSD([subQ0]),TDD([makeQuery(id+"F3.imprint","IMPRINT",EDGE,{"disambiguationData":[TD([[makeQuery(id+"F3.imprint","INTERSECT",VERTEX,{"derivedFrom":[sQuery(id+"F3.wireOp",EDGE,"E13"),sQuery(id+"F3.wireOp",EDGE,"E29"),subQ0]}),-1.0]])],"derivedFrom":subQ0})])],"isStart":false});}
            var Q4;
            {var subQ0=sQuery(id+"F3.wireOp",EDGE,"E13");Q4=makeQuery(id+"F4.opExtrude","CAP_EDGE",EDGE,{"disambiguationData":[OSD([subQ0]),TDD([makeQuery(id+"F3.imprint","IMPRINT",EDGE,{"disambiguationData":[TD([[makeQuery(id+"F3.imprint","INTERSECT",VERTEX,{"derivedFrom":[subQ0,sQuery(id+"F3.wireOp",EDGE,"E29"),sQuery(id+"F3.wireOp",EDGE,"E32")]}),-1.0]])],"derivedFrom":subQ0})])],"isStart":false});}
            var Q5;
            {var subQ0=sQuery(id+"F3.wireOp",EDGE,"E31");Q5=makeQuery(id+"F4.opExtrude","CAP_EDGE",EDGE,{"disambiguationData":[OSD([subQ0]),TDD([makeQuery(id+"F3.imprint","IMPRINT",EDGE,{"disambiguationData":[TD([[makeQuery(id+"F3.imprint","INTERSECT",VERTEX,{"derivedFrom":[sQuery(id+"F3.wireOp",EDGE,"E13"),subQ0,sQuery(id+"F3.wireOp",EDGE,"E37")]}),1.0]])],"derivedFrom":subQ0})])],"isStart":false});}
            var Q6;
            {var subQ0=sQuery(id+"F3.wireOp",EDGE,"E28");Q6=makeQuery(id+"F4.opExtrude","CAP_EDGE",EDGE,{"disambiguationData":[OSD([subQ0]),TDD([makeQuery(id+"F3.imprint","IMPRINT",EDGE,{"disambiguationData":[TD([[makeQuery(id+"F3.imprint","INTERSECT",VERTEX,{"derivedFrom":[subQ0,sQuery(id+"F3.wireOp",EDGE,"E35"),sQuery(id+"F3.wireOp",EDGE,"E54")]}),1.0]])],"derivedFrom":subQ0})])],"isStart":false});}
            var Q7;
            Q7=makeQuery(id+"F4.opExtrude","CAP_FACE",FACE,{"disambiguationData":[OSD([sQuery(id+"F3.wireOp",EDGE,"E28"),sQuery(id+"F3.wireOp",EDGE,"E30"),sQuery(id+"F3.wireOp",EDGE,"E54")])],"isStart":false});
            var Q8;
            {var subQ0=sQuery(id+"F3.wireOp",EDGE,"E33");Q8=makeQuery(id+"F4.opExtrude","CAP_EDGE",EDGE,{"disambiguationData":[OSD([subQ0]),TDD([makeQuery(id+"F3.imprint","IMPRINT",EDGE,{"disambiguationData":[TD([[makeQuery(id+"F3.imprint","INTERSECT",VERTEX,{"derivedFrom":[sQuery(id+"F3.wireOp",EDGE,"E20"),sQuery(id+"F3.wireOp",EDGE,"E32"),subQ0]}),-1.0]])],"derivedFrom":subQ0})])],"isStart":false});}
            var Q9;
            {var subQ0=sQuery(id+"F3.wireOp",EDGE,"E54");Q9=makeQuery(id+"F4.opExtrude","CAP_EDGE",EDGE,{"disambiguationData":[OSD([subQ0]),TDD([makeQuery(id+"F3.imprint","IMPRINT",EDGE,{"disambiguationData":[TD([[makeQuery(id+"F3.imprint","INTERSECT",VERTEX,{"derivedFrom":[sQuery(id+"F3.wireOp",EDGE,"E30"),sQuery(id+"F3.wireOp",EDGE,"E33"),subQ0]}),-1.0]])],"derivedFrom":subQ0})])],"isStart":false});}
            var Q10;
            {var subQ0=sQuery(id+"F3.wireOp",EDGE,"E32");Q10=makeQuery(id+"F4.opExtrude","CAP_EDGE",EDGE,{"disambiguationData":[OSD([subQ0]),TDD([makeQuery(id+"F3.imprint","IMPRINT",EDGE,{"disambiguationData":[TD([[makeQuery(id+"F3.imprint","INTERSECT",VERTEX,{"derivedFrom":[sQuery(id+"F3.wireOp",EDGE,"E20"),subQ0,sQuery(id+"F3.wireOp",EDGE,"E33")]}),-1.0]])],"derivedFrom":subQ0})])],"isStart":false});}
            var Q11;
            {var subQ0=sQuery(id+"F3.wireOp",EDGE,"E33");Q11=makeQuery(id+"F4.opExtrude","CAP_EDGE",EDGE,{"disambiguationData":[OSD([subQ0]),TDD([makeQuery(id+"F3.imprint","IMPRINT",EDGE,{"disambiguationData":[TD([[makeQuery(id+"F3.imprint","INTERSECT",VERTEX,{"derivedFrom":[sQuery(id+"F3.wireOp",EDGE,"E21"),subQ0,sQuery(id+"F3.wireOp",EDGE,"E35")]}),-1.0]])],"derivedFrom":subQ0})])],"isStart":false});}
            var Q12;
            {var subQ0=sQuery(id+"F3.wireOp",EDGE,"E35");Q12=makeQuery(id+"F4.opExtrude","CAP_EDGE",EDGE,{"disambiguationData":[OSD([subQ0]),TDD([makeQuery(id+"F3.imprint","IMPRINT",EDGE,{"disambiguationData":[TD([[makeQuery(id+"F3.imprint","INTERSECT",VERTEX,{"derivedFrom":[sQuery(id+"F3.wireOp",EDGE,"E21"),sQuery(id+"F3.wireOp",EDGE,"E33"),subQ0]}),-1.0]])],"derivedFrom":subQ0})])],"isStart":false});}
            var Q13;
            {var subQ0=sQuery(id+"F3.wireOp",EDGE,"E58");Q13=makeQuery(id+"F4.opExtrude","CAP_EDGE",EDGE,{"disambiguationData":[OSD([subQ0]),TDD([makeQuery(id+"F3.imprint","IMPRINT",EDGE,{"disambiguationData":[TD([[makeQuery(id+"F3.imprint","INTERSECT",VERTEX,{"derivedFrom":[sQuery(id+"F3.wireOp",EDGE,"E33"),sQuery(id+"F3.wireOp",EDGE,"E36"),subQ0]}),-1.0]])],"derivedFrom":subQ0})])],"isStart":false});}
            var Q14;
            {var subQ0=sQuery(id+"F3.wireOp",EDGE,"E34");Q14=makeQuery(id+"F4.opExtrude","CAP_EDGE",EDGE,{"disambiguationData":[OSD([subQ0]),TDD([makeQuery(id+"F3.imprint","IMPRINT",EDGE,{"disambiguationData":[TD([[makeQuery(id+"F3.imprint","INTERSECT",VERTEX,{"derivedFrom":[sQuery(id+"F3.wireOp",EDGE,"E21"),sQuery(id+"F3.wireOp",EDGE,"E30"),subQ0]}),-1.0]])],"derivedFrom":subQ0})])],"isStart":false});}
            var Q15;
            {var subQ0=sQuery(id+"F3.wireOp",EDGE,"E30");Q15=makeQuery(id+"F4.opExtrude","CAP_EDGE",EDGE,{"disambiguationData":[OSD([subQ0]),TDD([makeQuery(id+"F3.imprint","IMPRINT",EDGE,{"disambiguationData":[TD([[makeQuery(id+"F3.imprint","INTERSECT",VERTEX,{"derivedFrom":[sQuery(id+"F3.wireOp",EDGE,"E21"),subQ0,sQuery(id+"F3.wireOp",EDGE,"E34")]}),-1.0]])],"derivedFrom":subQ0})])],"isStart":false});}
            var Q16;
            {var subQ0=sQuery(id+"F3.wireOp",EDGE,"E58");Q16=makeQuery(id+"F4.opExtrude","CAP_EDGE",EDGE,{"disambiguationData":[OSD([subQ0]),TDD([makeQuery(id+"F3.imprint","IMPRINT",EDGE,{"disambiguationData":[TD([[makeQuery(id+"F3.imprint","INTERSECT",VERTEX,{"derivedFrom":[sQuery(id+"F3.wireOp",EDGE,"E30"),sQuery(id+"F3.wireOp",EDGE,"E39"),subQ0]}),1.0]])],"derivedFrom":subQ0})])],"isStart":false});}
            chamfer(context, id + "F5", {"entities" : qUnion([Q0, Q1, Q2, Q3, Q4, Q5, Q6, Q7, Q8, Q9, Q10, Q11, Q12, Q13, Q14, Q15, Q16]), "chamferType" : ChamferType.OFFSET_ANGLE, "width" : 3 * mm, "oppositeDirection" : false, "angle" : 59 * degree, "tangentPropagation" : true});
        }
        {
            var Q0;
            {var subQ0=sQuery(id+"F3.wireOp",EDGE,"E29");Q0=makeQuery(id+"F4.opExtrude","CAP_EDGE",EDGE,{"disambiguationData":[OSD([subQ0]),TDD([makeQuery(id+"F3.imprint","IMPRINT",EDGE,{"disambiguationData":[TD([[makeQuery(id+"F3.imprint","INTERSECT",VERTEX,{"derivedFrom":[subQ0,sQuery(id+"F3.wireOp",EDGE,"E30"),sQuery(id+"F3.wireOp",EDGE,"E56")]}),1.0]])],"derivedFrom":subQ0})])],"isStart":false});}
            var Q1;
            {var subQ0=sQuery(id+"F3.wireOp",EDGE,"E20");Q1=makeQuery(id+"F4.opExtrude","CAP_EDGE",EDGE,{"disambiguationData":[OSD([subQ0]),TDD([makeQuery(id+"F3.imprint","IMPRINT",EDGE,{"disambiguationData":[TD([[makeQuery(id+"F3.imprint","INTERSECT",VERTEX,{"derivedFrom":[sQuery(id+"F3.wireOp",EDGE,"E10"),subQ0,sQuery(id+"F3.wireOp",EDGE,"E29"),sQuery(id+"F3.wireOp",EDGE,"E35")]}),-1.0]])],"derivedFrom":subQ0})])],"isStart":false});}
            var Q2;
            Q2=makeQuery(id+"F4.opExtrude","CAP_FACE",FACE,{"disambiguationData":[OSD([sQuery(id+"F3.wireOp",EDGE,"E20"),sQuery(id+"F3.wireOp",EDGE,"E29"),sQuery(id+"F3.wireOp",EDGE,"E30")])],"isStart":false});
            var Q3;
            {var subQ0=sQuery(id+"F3.wireOp",EDGE,"E31");Q3=makeQuery(id+"F4.opExtrude","CAP_EDGE",EDGE,{"disambiguationData":[OSD([subQ0]),TDD([makeQuery(id+"F3.imprint","IMPRINT",EDGE,{"disambiguationData":[TD([[makeQuery(id+"F3.imprint","INTERSECT",VERTEX,{"derivedFrom":[subQ0,sQuery(id+"F3.wireOp",EDGE,"E32"),sQuery(id+"F3.wireOp",EDGE,"E56")]}),1.0]])],"derivedFrom":subQ0})])],"isStart":false});}
            var Q4;
            Q4=makeQuery(id+"F4.opExtrude","CAP_FACE",FACE,{"disambiguationData":[OSD([sQuery(id+"F3.wireOp",EDGE,"E20"),sQuery(id+"F3.wireOp",EDGE,"E31"),sQuery(id+"F3.wireOp",EDGE,"E32")])],"isStart":false});
            var Q5;
            {var subQ0=sQuery(id+"F3.wireOp",EDGE,"E35");Q5=makeQuery(id+"F4.opExtrude","CAP_EDGE",EDGE,{"disambiguationData":[OSD([subQ0]),TDD([makeQuery(id+"F3.imprint","IMPRINT",EDGE,{"disambiguationData":[TD([[makeQuery(id+"F3.imprint","INTERSECT",VERTEX,{"derivedFrom":[sQuery(id+"F3.wireOp",EDGE,"E21"),sQuery(id+"F3.wireOp",EDGE,"E33"),subQ0]}),1.0]])],"derivedFrom":subQ0})])],"isStart":false});}
            var Q6;
            {var subQ0=sQuery(id+"F3.wireOp",EDGE,"E28");Q6=makeQuery(id+"F4.opExtrude","CAP_EDGE",EDGE,{"disambiguationData":[OSD([subQ0]),TDD([makeQuery(id+"F3.imprint","IMPRINT",EDGE,{"disambiguationData":[TD([[makeQuery(id+"F3.imprint","INTERSECT",VERTEX,{"derivedFrom":[subQ0,sQuery(id+"F3.wireOp",EDGE,"E35"),sQuery(id+"F3.wireOp",EDGE,"E54")]}),-1.0]])],"derivedFrom":subQ0})])],"isStart":false});}
            var Q7;
            {var subQ0=sQuery(id+"F3.wireOp",EDGE,"E21");Q7=makeQuery(id+"F4.opExtrude","CAP_EDGE",EDGE,{"disambiguationData":[OSD([subQ0]),TDD([makeQuery(id+"F3.imprint","IMPRINT",EDGE,{"disambiguationData":[TD([[makeQuery(id+"F3.imprint","INTERSECT",VERTEX,{"derivedFrom":[subQ0,sQuery(id+"F3.wireOp",EDGE,"E33"),sQuery(id+"F3.wireOp",EDGE,"E35")]}),1.0]])],"derivedFrom":subQ0})])],"isStart":false});}
            var Q8;
            {var subQ0=sQuery(id+"F3.wireOp",EDGE,"E30");Q8=makeQuery(id+"F4.opExtrude","CAP_EDGE",EDGE,{"disambiguationData":[OSD([subQ0]),TDD([makeQuery(id+"F3.imprint","IMPRINT",EDGE,{"disambiguationData":[TD([[makeQuery(id+"F3.imprint","INTERSECT",VERTEX,{"derivedFrom":[sQuery(id+"F3.wireOp",EDGE,"E21"),subQ0,sQuery(id+"F3.wireOp",EDGE,"E34")]}),1.0]])],"derivedFrom":subQ0})])],"isStart":false});}
            var Q9;
            {var subQ0=sQuery(id+"F3.wireOp",EDGE,"E33");Q9=makeQuery(id+"F4.opExtrude","CAP_EDGE",EDGE,{"disambiguationData":[OSD([subQ0]),TDD([makeQuery(id+"F3.imprint","IMPRINT",EDGE,{"disambiguationData":[TD([[makeQuery(id+"F3.imprint","INTERSECT",VERTEX,{"derivedFrom":[sQuery(id+"F3.wireOp",EDGE,"E21"),subQ0,sQuery(id+"F3.wireOp",EDGE,"E35")]}),1.0]])],"derivedFrom":subQ0})])],"isStart":false});}
            var Q10;
            {var subQ0=sQuery(id+"F3.wireOp",EDGE,"E21");Q10=makeQuery(id+"F4.opExtrude","CAP_EDGE",EDGE,{"disambiguationData":[OSD([subQ0]),TDD([makeQuery(id+"F3.imprint","IMPRINT",EDGE,{"disambiguationData":[TD([[makeQuery(id+"F3.imprint","INTERSECT",VERTEX,{"derivedFrom":[subQ0,sQuery(id+"F3.wireOp",EDGE,"E33"),sQuery(id+"F3.wireOp",EDGE,"E35")]}),-1.0]])],"derivedFrom":subQ0})])],"isStart":false});}
            chamfer(context, id + "F6", {"entities" : qUnion([Q0, Q1, Q2, Q3, Q4, Q5, Q6, Q7, Q8, Q9, Q10]), "chamferType" : ChamferType.OFFSET_ANGLE, "width" : 3 * mm, "oppositeDirection" : true, "angle" : 59 * degree, "tangentPropagation" : true});
        }
        {
            var Q0;
            {var subQ0=sQuery(id+"F3.wireOp",EDGE,"E33");Q0=makeQuery(id+"F4.opExtrude","CAP_EDGE",EDGE,{"disambiguationData":[OSD([subQ0]),TDD([makeQuery(id+"F3.imprint","IMPRINT",EDGE,{"disambiguationData":[TD([[makeQuery(id+"F3.imprint","INTERSECT",VERTEX,{"derivedFrom":[sQuery(id+"F3.wireOp",EDGE,"E10"),sQuery(id+"F3.wireOp",EDGE,"E11"),subQ0]}),1.0]])],"derivedFrom":subQ0})])],"isStart":false});}
            var Q1;
            {var subQ0=sQuery(id+"F3.wireOp",EDGE,"E11");Q1=makeQuery(id+"F4.opExtrude","CAP_EDGE",EDGE,{"disambiguationData":[OSD([subQ0]),TDD([makeQuery(id+"F3.imprint","IMPRINT",EDGE,{"disambiguationData":[TD([[makeQuery(id+"F3.imprint","INTERSECT",VERTEX,{"derivedFrom":[sQuery(id+"F3.wireOp",EDGE,"E10"),subQ0,sQuery(id+"F3.wireOp",EDGE,"E33")]}),-1.0]])],"derivedFrom":subQ0})])],"isStart":false});}
            var Q2;
            {var subQ0=sQuery(id+"F3.wireOp",EDGE,"E36");Q2=makeQuery(id+"F4.opExtrude","CAP_EDGE",EDGE,{"disambiguationData":[OSD([subQ0]),TDD([makeQuery(id+"F3.imprint","IMPRINT",EDGE,{"disambiguationData":[TD([[makeQuery(id+"F3.imprint","INTERSECT",VERTEX,{"derivedFrom":[sQuery(id+"F3.wireOp",EDGE,"E11"),sQuery(id+"F3.wireOp",EDGE,"E34"),subQ0]}),1.0]])],"derivedFrom":subQ0})])],"isStart":false});}
            var Q3;
            {var subQ0=sQuery(id+"F3.wireOp",EDGE,"E34");Q3=makeQuery(id+"F4.opExtrude","CAP_EDGE",EDGE,{"disambiguationData":[OSD([subQ0]),TDD([makeQuery(id+"F3.imprint","IMPRINT",EDGE,{"disambiguationData":[TD([[makeQuery(id+"F3.imprint","INTERSECT",VERTEX,{"derivedFrom":[sQuery(id+"F3.wireOp",EDGE,"E11"),subQ0,sQuery(id+"F3.wireOp",EDGE,"E36")]}),1.0]])],"derivedFrom":subQ0})])],"isStart":false});}
            var Q4;
            {var subQ0=sQuery(id+"F3.wireOp",EDGE,"E11");Q4=makeQuery(id+"F4.opExtrude","CAP_EDGE",EDGE,{"disambiguationData":[OSD([subQ0]),TDD([makeQuery(id+"F3.imprint","IMPRINT",EDGE,{"disambiguationData":[TD([[makeQuery(id+"F3.imprint","INTERSECT",VERTEX,{"derivedFrom":[subQ0,sQuery(id+"F3.wireOp",EDGE,"E34"),sQuery(id+"F3.wireOp",EDGE,"E36")]}),-1.0]])],"derivedFrom":subQ0})])],"isStart":false});}
            var Q5;
            {var subQ0=sQuery(id+"F3.wireOp",EDGE,"E35");Q5=makeQuery(id+"F4.opExtrude","CAP_EDGE",EDGE,{"disambiguationData":[OSD([subQ0]),TDD([makeQuery(id+"F3.imprint","IMPRINT",EDGE,{"disambiguationData":[TD([[makeQuery(id+"F3.imprint","INTERSECT",VERTEX,{"derivedFrom":[sQuery(id+"F3.wireOp",EDGE,"E11"),subQ0,sQuery(id+"F3.wireOp",EDGE,"E39")]}),1.0]])],"derivedFrom":subQ0})])],"isStart":false});}
            var Q6;
            {var subQ0=sQuery(id+"F3.wireOp",EDGE,"E21");Q6=makeQuery(id+"F4.opExtrude","CAP_EDGE",EDGE,{"disambiguationData":[OSD([subQ0]),TDD([makeQuery(id+"F3.imprint","IMPRINT",EDGE,{"disambiguationData":[TD([[makeQuery(id+"F3.imprint","INTERSECT",VERTEX,{"derivedFrom":[subQ0,sQuery(id+"F3.wireOp",EDGE,"E30"),sQuery(id+"F3.wireOp",EDGE,"E34")]}),-1.0]])],"derivedFrom":subQ0})])],"isStart":false});}
            var Q7;
            {var subQ0=sQuery(id+"F3.wireOp",EDGE,"E34");Q7=makeQuery(id+"F4.opExtrude","CAP_EDGE",EDGE,{"disambiguationData":[OSD([subQ0]),TDD([makeQuery(id+"F3.imprint","IMPRINT",EDGE,{"disambiguationData":[TD([[makeQuery(id+"F3.imprint","INTERSECT",VERTEX,{"derivedFrom":[sQuery(id+"F3.wireOp",EDGE,"E21"),sQuery(id+"F3.wireOp",EDGE,"E30"),subQ0]}),1.0]])],"derivedFrom":subQ0})])],"isStart":false});}
            var Q8;
            {var subQ0=sQuery(id+"F3.wireOp",EDGE,"E32");Q8=makeQuery(id+"F4.opExtrude","CAP_EDGE",EDGE,{"disambiguationData":[OSD([subQ0]),TDD([makeQuery(id+"F3.imprint","IMPRINT",EDGE,{"disambiguationData":[TD([[makeQuery(id+"F3.imprint","INTERSECT",VERTEX,{"derivedFrom":[sQuery(id+"F3.wireOp",EDGE,"E21"),subQ0,sQuery(id+"F3.wireOp",EDGE,"E39")]}),1.0]])],"derivedFrom":subQ0})])],"isStart":false});}
            var Q9;
            {var subQ0=sQuery(id+"F3.wireOp",EDGE,"E20");Q9=makeQuery(id+"F4.opExtrude","CAP_EDGE",EDGE,{"disambiguationData":[OSD([subQ0]),TDD([makeQuery(id+"F3.imprint","IMPRINT",EDGE,{"disambiguationData":[TD([[makeQuery(id+"F3.imprint","INTERSECT",VERTEX,{"derivedFrom":[subQ0,sQuery(id+"F3.wireOp",EDGE,"E32"),sQuery(id+"F3.wireOp",EDGE,"E33")]}),-1.0]])],"derivedFrom":subQ0})])],"isStart":false});}
            var Q10;
            {var subQ0=sQuery(id+"F3.wireOp",EDGE,"E33");Q10=makeQuery(id+"F4.opExtrude","CAP_EDGE",EDGE,{"disambiguationData":[OSD([subQ0]),TDD([makeQuery(id+"F3.imprint","IMPRINT",EDGE,{"disambiguationData":[TD([[makeQuery(id+"F3.imprint","INTERSECT",VERTEX,{"derivedFrom":[sQuery(id+"F3.wireOp",EDGE,"E20"),sQuery(id+"F3.wireOp",EDGE,"E32"),subQ0]}),1.0]])],"derivedFrom":subQ0})])],"isStart":false});}
            var Q11;
            {var subQ0=sQuery(id+"F3.wireOp",EDGE,"E37");Q11=makeQuery(id+"F4.opExtrude","CAP_EDGE",EDGE,{"disambiguationData":[OSD([subQ0]),TDD([makeQuery(id+"F3.imprint","IMPRINT",EDGE,{"disambiguationData":[TD([[makeQuery(id+"F3.imprint","INTERSECT",VERTEX,{"derivedFrom":[sQuery(id+"F3.wireOp",EDGE,"E20"),sQuery(id+"F3.wireOp",EDGE,"E34"),subQ0]}),1.0]])],"derivedFrom":subQ0})])],"isStart":false});}
            var Q12;
            {var subQ0=sQuery(id+"F3.wireOp",EDGE,"E37");Q12=makeQuery(id+"F4.opExtrude","CAP_EDGE",EDGE,{"disambiguationData":[OSD([subQ0]),TDD([makeQuery(id+"F3.imprint","IMPRINT",EDGE,{"disambiguationData":[TD([[makeQuery(id+"F3.imprint","INTERSECT",VERTEX,{"derivedFrom":[sQuery(id+"F3.wireOp",EDGE,"E13"),sQuery(id+"F3.wireOp",EDGE,"E31"),subQ0]}),-1.0]])],"derivedFrom":subQ0})])],"isStart":false});}
            var Q13;
            {var subQ0=sQuery(id+"F3.wireOp",EDGE,"E33");Q13=makeQuery(id+"F4.opExtrude","CAP_EDGE",EDGE,{"disambiguationData":[OSD([subQ0]),TDD([makeQuery(id+"F3.imprint","IMPRINT",EDGE,{"disambiguationData":[TD([[makeQuery(id+"F3.imprint","INTERSECT",VERTEX,{"derivedFrom":[sQuery(id+"F3.wireOp",EDGE,"E13"),subQ0,sQuery(id+"F3.wireOp",EDGE,"E38")]}),-1.0]])],"derivedFrom":subQ0})])],"isStart":false});}
            var Q14;
            {var subQ0=sQuery(id+"F3.wireOp",EDGE,"E13");Q14=makeQuery(id+"F4.opExtrude","CAP_EDGE",EDGE,{"disambiguationData":[OSD([subQ0]),TDD([makeQuery(id+"F3.imprint","IMPRINT",EDGE,{"disambiguationData":[TD([[makeQuery(id+"F3.imprint","INTERSECT",VERTEX,{"derivedFrom":[subQ0,sQuery(id+"F3.wireOp",EDGE,"E31"),sQuery(id+"F3.wireOp",EDGE,"E37")]}),-1.0]])],"derivedFrom":subQ0})])],"isStart":false});}
            var Q15;
            {var subQ0=sQuery(id+"F3.wireOp",EDGE,"E54");Q15=makeQuery(id+"F4.opExtrude","CAP_EDGE",EDGE,{"disambiguationData":[OSD([subQ0]),TDD([makeQuery(id+"F3.imprint","IMPRINT",EDGE,{"disambiguationData":[TD([[makeQuery(id+"F3.imprint","INTERSECT",VERTEX,{"derivedFrom":[sQuery(id+"F3.wireOp",EDGE,"E32"),sQuery(id+"F3.wireOp",EDGE,"E34"),subQ0]}),-1.0]])],"derivedFrom":subQ0})])],"isStart":false});}
            var Q16;
            {var subQ0=sQuery(id+"F3.wireOp",EDGE,"E34");Q16=makeQuery(id+"F4.opExtrude","CAP_EDGE",EDGE,{"disambiguationData":[OSD([subQ0]),TDD([makeQuery(id+"F3.imprint","IMPRINT",EDGE,{"disambiguationData":[TD([[makeQuery(id+"F3.imprint","INTERSECT",VERTEX,{"derivedFrom":[sQuery(id+"F3.wireOp",EDGE,"E20"),subQ0,sQuery(id+"F3.wireOp",EDGE,"E37")]}),-1.0]])],"derivedFrom":subQ0})])],"isStart":false});}
            var Q17;
            {var subQ0=sQuery(id+"F3.wireOp",EDGE,"E37");Q17=makeQuery(id+"F4.opExtrude","CAP_EDGE",EDGE,{"disambiguationData":[OSD([subQ0]),TDD([makeQuery(id+"F3.imprint","IMPRINT",EDGE,{"disambiguationData":[TD([[makeQuery(id+"F3.imprint","INTERSECT",VERTEX,{"derivedFrom":[sQuery(id+"F3.wireOp",EDGE,"E20"),sQuery(id+"F3.wireOp",EDGE,"E34"),subQ0]}),-1.0]])],"derivedFrom":subQ0})])],"isStart":false});}
            var Q18;
            {var subQ0=sQuery(id+"F3.wireOp",EDGE,"E38");Q18=makeQuery(id+"F4.opExtrude","CAP_EDGE",EDGE,{"disambiguationData":[OSD([subQ0]),TDD([makeQuery(id+"F3.imprint","IMPRINT",EDGE,{"disambiguationData":[TD([[makeQuery(id+"F3.imprint","INTERSECT",VERTEX,{"derivedFrom":[sQuery(id+"F3.wireOp",EDGE,"E13"),sQuery(id+"F3.wireOp",EDGE,"E33"),subQ0]}),-1.0]])],"derivedFrom":subQ0})])],"isStart":false});}
            var Q19;
            {var subQ0=sQuery(id+"F3.wireOp",EDGE,"E34");Q19=makeQuery(id+"F4.opExtrude","CAP_EDGE",EDGE,{"disambiguationData":[OSD([subQ0]),TDD([makeQuery(id+"F3.imprint","IMPRINT",EDGE,{"disambiguationData":[TD([[makeQuery(id+"F3.imprint","INTERSECT",VERTEX,{"derivedFrom":[sQuery(id+"F3.wireOp",EDGE,"E13"),subQ0,sQuery(id+"F3.wireOp",EDGE,"E43")]}),-1.0]])],"derivedFrom":subQ0})])],"isStart":false});}
            var Q20;
            {var subQ0=sQuery(id+"F3.wireOp",EDGE,"E13");Q20=makeQuery(id+"F4.opExtrude","CAP_EDGE",EDGE,{"disambiguationData":[OSD([subQ0]),TDD([makeQuery(id+"F3.imprint","IMPRINT",EDGE,{"disambiguationData":[TD([[makeQuery(id+"F3.imprint","INTERSECT",VERTEX,{"derivedFrom":[subQ0,sQuery(id+"F3.wireOp",EDGE,"E33"),sQuery(id+"F3.wireOp",EDGE,"E38")]}),-1.0]])],"derivedFrom":subQ0})])],"isStart":false});}
            var Q21;
            {var subQ0=sQuery(id+"F3.wireOp",EDGE,"E43");Q21=makeQuery(id+"F4.opExtrude","CAP_EDGE",EDGE,{"disambiguationData":[OSD([subQ0]),TDD([makeQuery(id+"F3.imprint","IMPRINT",EDGE,{"disambiguationData":[TD([[makeQuery(id+"F3.imprint","INTERSECT",VERTEX,{"derivedFrom":[sQuery(id+"F3.wireOp",EDGE,"E13"),sQuery(id+"F3.wireOp",EDGE,"E34"),subQ0]}),-1.0]])],"derivedFrom":subQ0})])],"isStart":false});}
            var Q22;
            {var subQ0=sQuery(id+"F3.wireOp",EDGE,"E42");Q22=makeQuery(id+"F4.opExtrude","CAP_EDGE",EDGE,{"disambiguationData":[OSD([subQ0]),TDD([makeQuery(id+"F3.imprint","IMPRINT",EDGE,{"disambiguationData":[TD([[makeQuery(id+"F3.imprint","INTERSECT",VERTEX,{"derivedFrom":[sQuery(id+"F3.wireOp",EDGE,"E13"),subQ0,sQuery(id+"F3.wireOp",EDGE,"E44")]}),-1.0]])],"derivedFrom":subQ0})])],"isStart":false});}
            var Q23;
            {var subQ0=sQuery(id+"F3.wireOp",EDGE,"E13");Q23=makeQuery(id+"F4.opExtrude","CAP_EDGE",EDGE,{"disambiguationData":[OSD([subQ0]),TDD([makeQuery(id+"F3.imprint","IMPRINT",EDGE,{"disambiguationData":[TD([[makeQuery(id+"F3.imprint","INTERSECT",VERTEX,{"derivedFrom":[subQ0,sQuery(id+"F3.wireOp",EDGE,"E34"),sQuery(id+"F3.wireOp",EDGE,"E43")]}),-1.0]])],"derivedFrom":subQ0})])],"isStart":false});}
            var Q24;
            {var subQ0=sQuery(id+"F3.wireOp",EDGE,"E44");Q24=makeQuery(id+"F4.opExtrude","CAP_EDGE",EDGE,{"disambiguationData":[OSD([subQ0]),TDD([makeQuery(id+"F3.imprint","IMPRINT",EDGE,{"disambiguationData":[TD([[makeQuery(id+"F3.imprint","INTERSECT",VERTEX,{"derivedFrom":[sQuery(id+"F3.wireOp",EDGE,"E40"),subQ0]}),1.0]])],"derivedFrom":subQ0})])],"isStart":false});}
            var Q25;
            {var subQ0=sQuery(id+"F3.wireOp",EDGE,"E40");Q25=makeQuery(id+"F4.opExtrude","CAP_EDGE",EDGE,{"disambiguationData":[OSD([subQ0]),TDD([makeQuery(id+"F3.imprint","IMPRINT",EDGE,{"disambiguationData":[TD([[makeQuery(id+"F3.imprint","INTERSECT",VERTEX,{"derivedFrom":[subQ0,sQuery(id+"F3.wireOp",EDGE,"E44")]}),-1.0]])],"derivedFrom":subQ0})])],"isStart":false});}
            var Q26;
            {var subQ0=sQuery(id+"F3.wireOp",EDGE,"E13");Q26=makeQuery(id+"F4.opExtrude","CAP_EDGE",EDGE,{"disambiguationData":[OSD([subQ0]),TDD([makeQuery(id+"F3.imprint","IMPRINT",EDGE,{"disambiguationData":[TD([[makeQuery(id+"F3.imprint","INTERSECT",VERTEX,{"derivedFrom":[subQ0,sQuery(id+"F3.wireOp",EDGE,"E40"),sQuery(id+"F3.wireOp",EDGE,"E46")]}),1.0]])],"derivedFrom":subQ0})])],"isStart":false});}
            var Q27;
            {var subQ0=sQuery(id+"F3.wireOp",EDGE,"E46");Q27=makeQuery(id+"F4.opExtrude","CAP_EDGE",EDGE,{"disambiguationData":[OSD([subQ0]),TDD([makeQuery(id+"F3.imprint","IMPRINT",EDGE,{"disambiguationData":[TD([[makeQuery(id+"F3.imprint","INTERSECT",VERTEX,{"derivedFrom":[subQ0,sQuery(id+"F3.wireOp",EDGE,"E56")]}),1.0]])],"derivedFrom":subQ0})])],"isStart":false});}
            var Q28;
            {var subQ0=sQuery(id+"F3.wireOp",EDGE,"E13");Q28=makeQuery(id+"F4.opExtrude","CAP_EDGE",EDGE,{"disambiguationData":[OSD([subQ0]),TDD([makeQuery(id+"F3.imprint","IMPRINT",EDGE,{"disambiguationData":[TD([[makeQuery(id+"F3.imprint","INTERSECT",VERTEX,{"derivedFrom":[sQuery(id+"F3.wireOp",EDGE,"E12"),subQ0,sQuery(id+"F3.wireOp",EDGE,"E41")]}),1.0]])],"derivedFrom":subQ0})])],"isStart":false});}
            var Q29;
            {var subQ0=sQuery(id+"F3.wireOp",EDGE,"E41");Q29=makeQuery(id+"F4.opExtrude","CAP_EDGE",EDGE,{"disambiguationData":[OSD([subQ0]),TDD([makeQuery(id+"F3.imprint","IMPRINT",EDGE,{"disambiguationData":[TD([[makeQuery(id+"F3.imprint","INTERSECT",VERTEX,{"derivedFrom":[subQ0,sQuery(id+"F3.wireOp",EDGE,"E56")]}),1.0]])],"derivedFrom":subQ0})])],"isStart":false});}
            var Q30;
            {var subQ0=sQuery(id+"F3.wireOp",EDGE,"E42");Q30=makeQuery(id+"F4.opExtrude","CAP_EDGE",EDGE,{"disambiguationData":[OSD([subQ0]),TDD([makeQuery(id+"F3.imprint","IMPRINT",EDGE,{"disambiguationData":[TD([[makeQuery(id+"F3.imprint","INTERSECT",VERTEX,{"derivedFrom":[subQ0,sQuery(id+"F3.wireOp",EDGE,"E43"),sQuery(id+"F3.wireOp",EDGE,"E56")]}),-1.0]])],"derivedFrom":subQ0})])],"isStart":false});}
            var Q31;
            {var subQ0=sQuery(id+"F3.wireOp",EDGE,"E20");Q31=makeQuery(id+"F4.opExtrude","CAP_EDGE",EDGE,{"disambiguationData":[OSD([subQ0]),TDD([makeQuery(id+"F3.imprint","IMPRINT",EDGE,{"disambiguationData":[TD([[makeQuery(id+"F3.imprint","INTERSECT",VERTEX,{"derivedFrom":[subQ0,sQuery(id+"F3.wireOp",EDGE,"E40"),sQuery(id+"F3.wireOp",EDGE,"E43"),sQuery(id+"F3.wireOp",EDGE,"E50")]}),1.0]])],"derivedFrom":subQ0})])],"isStart":false});}
            var Q32;
            {var subQ0=sQuery(id+"F3.wireOp",EDGE,"E43");Q32=makeQuery(id+"F4.opExtrude","CAP_EDGE",EDGE,{"disambiguationData":[OSD([subQ0]),TDD([makeQuery(id+"F3.imprint","IMPRINT",EDGE,{"disambiguationData":[TD([[makeQuery(id+"F3.imprint","INTERSECT",VERTEX,{"derivedFrom":[sQuery(id+"F3.wireOp",EDGE,"E42"),subQ0,sQuery(id+"F3.wireOp",EDGE,"E56")]}),-1.0]])],"derivedFrom":subQ0})])],"isStart":false});}
            var Q33;
            {var subQ0=sQuery(id+"F3.wireOp",EDGE,"E41");Q33=makeQuery(id+"F4.opExtrude","CAP_EDGE",EDGE,{"disambiguationData":[OSD([subQ0]),TDD([makeQuery(id+"F3.imprint","IMPRINT",EDGE,{"disambiguationData":[TD([[makeQuery(id+"F3.imprint","INTERSECT",VERTEX,{"derivedFrom":[subQ0,sQuery(id+"F3.wireOp",EDGE,"E46")]}),-1.0]])],"derivedFrom":subQ0})])],"isStart":false});}
            var Q34;
            {var subQ0=sQuery(id+"F3.wireOp",EDGE,"E20");Q34=makeQuery(id+"F4.opExtrude","CAP_EDGE",EDGE,{"disambiguationData":[OSD([subQ0]),TDD([makeQuery(id+"F3.imprint","IMPRINT",EDGE,{"disambiguationData":[TD([[makeQuery(id+"F3.imprint","INTERSECT",VERTEX,{"derivedFrom":[subQ0,sQuery(id+"F3.wireOp",EDGE,"E41"),sQuery(id+"F3.wireOp",EDGE,"E44")]}),-1.0]])],"derivedFrom":subQ0})])],"isStart":false});}
            var Q35;
            {var subQ0=sQuery(id+"F3.wireOp",EDGE,"E46");Q35=makeQuery(id+"F4.opExtrude","CAP_EDGE",EDGE,{"disambiguationData":[OSD([subQ0]),TDD([makeQuery(id+"F3.imprint","IMPRINT",EDGE,{"disambiguationData":[TD([[makeQuery(id+"F3.imprint","INTERSECT",VERTEX,{"derivedFrom":[sQuery(id+"F3.wireOp",EDGE,"E41"),subQ0]}),-1.0]])],"derivedFrom":subQ0})])],"isStart":false});}
            var Q36;
            {var subQ0=sQuery(id+"F3.wireOp",EDGE,"E54");Q36=makeQuery(id+"F4.opExtrude","CAP_EDGE",EDGE,{"disambiguationData":[OSD([subQ0]),TDD([makeQuery(id+"F3.imprint","IMPRINT",EDGE,{"disambiguationData":[TD([[makeQuery(id+"F3.imprint","INTERSECT",VERTEX,{"derivedFrom":[sQuery(id+"F3.wireOp",EDGE,"E41"),subQ0]}),-1.0]])],"derivedFrom":subQ0})])],"isStart":false});}
            var Q37;
            Q37=makeQuery(id+"F4.opExtrude","CAP_FACE",FACE,{"disambiguationData":[OSD([sQuery(id+"F3.wireOp",EDGE,"E41"),sQuery(id+"F3.wireOp",EDGE,"E44"),sQuery(id+"F3.wireOp",EDGE,"E54")])],"isStart":false});
            var Q38;
            {var subQ0=sQuery(id+"F3.wireOp",EDGE,"E50");var subQ1=makeQuery(id+"F3.imprint","INTERSECT",VERTEX,{"derivedFrom":[sQuery(id+"F3.wireOp",EDGE,"E49"),subQ0]});Q38=makeQuery(id+"F4.opExtrude","CAP_EDGE",EDGE,{"disambiguationData":[OSD([subQ0]),TDD([makeQuery(id+"F3.imprint","IMPRINT",EDGE,{"disambiguationData":[TD([[subQ1,1.0]])],"derivedFrom":subQ0}),makeQuery(id+"F3.imprint","IMPRINT",EDGE,{"disambiguationData":[TD([[subQ1,-1.0]])],"derivedFrom":subQ0})])],"isStart":false});}
            var Q39;
            Q39=makeQuery(id+"F4.opExtrude","CAP_FACE",FACE,{"disambiguationData":[OSD([sQuery(id+"F3.wireOp",EDGE,"E40"),sQuery(id+"F3.wireOp",EDGE,"E47"),sQuery(id+"F3.wireOp",EDGE,"E50"),sQuery(id+"F3.wireOp",EDGE,"E54")])],"isStart":false});
            var Q40;
            {var subQ0=sQuery(id+"F3.wireOp",EDGE,"E50");var subQ1=makeQuery(id+"F3.imprint","INTERSECT",VERTEX,{"derivedFrom":[sQuery(id+"F3.wireOp",EDGE,"E45"),subQ0]});Q40=makeQuery(id+"F4.opExtrude","CAP_EDGE",EDGE,{"disambiguationData":[OSD([subQ0]),TDD([makeQuery(id+"F3.imprint","IMPRINT",EDGE,{"disambiguationData":[TD([[subQ1,1.0]])],"derivedFrom":subQ0}),makeQuery(id+"F3.imprint","IMPRINT",EDGE,{"disambiguationData":[TD([[subQ1,-1.0]])],"derivedFrom":subQ0})])],"isStart":false});}
            var Q41;
            {var subQ0=sQuery(id+"F3.wireOp",EDGE,"E48");Q41=makeQuery(id+"F4.opExtrude","CAP_EDGE",EDGE,{"disambiguationData":[OSD([subQ0]),TDD([makeQuery(id+"F3.imprint","IMPRINT",EDGE,{"disambiguationData":[TD([[makeQuery(id+"F3.imprint","INTERSECT",VERTEX,{"derivedFrom":[sQuery(id+"F3.wireOp",EDGE,"E44"),subQ0]}),-1.0]])],"derivedFrom":subQ0})])],"isStart":false});}
            var Q42;
            {var subQ0=sQuery(id+"F3.wireOp",EDGE,"E21");Q42=makeQuery(id+"F4.opExtrude","CAP_EDGE",EDGE,{"disambiguationData":[OSD([subQ0]),TDD([makeQuery(id+"F3.imprint","IMPRINT",EDGE,{"disambiguationData":[TD([[makeQuery(id+"F3.imprint","INTERSECT",VERTEX,{"derivedFrom":[sQuery(id+"F3.wireOp",EDGE,"E12"),subQ0,sQuery(id+"F3.wireOp",EDGE,"E52")]}),1.0]])],"derivedFrom":subQ0})])],"isStart":false});}
            var Q43;
            Q43=makeQuery(id+"F4.opExtrude","CAP_FACE",FACE,{"disambiguationData":[OSD([sQuery(id+"F3.wireOp",EDGE,"E12"),sQuery(id+"F3.wireOp",EDGE,"E21"),sQuery(id+"F3.wireOp",EDGE,"E44"),sQuery(id+"F3.wireOp",EDGE,"E48")])],"isStart":false});
            var Q44;
            {var subQ0=sQuery(id+"F3.wireOp",EDGE,"E51");Q44=makeQuery(id+"F4.opExtrude","CAP_EDGE",EDGE,{"disambiguationData":[OSD([subQ0]),TDD([makeQuery(id+"F3.imprint","IMPRINT",EDGE,{"disambiguationData":[TD([[makeQuery(id+"F3.imprint","INTERSECT",VERTEX,{"derivedFrom":[sQuery(id+"F3.wireOp",EDGE,"E50"),subQ0]}),-1.0]])],"derivedFrom":subQ0})])],"isStart":false});}
            var Q45;
            {var subQ0=sQuery(id+"F3.wireOp",EDGE,"E58");Q45=makeQuery(id+"F4.opExtrude","CAP_EDGE",EDGE,{"disambiguationData":[OSD([subQ0]),TDD([makeQuery(id+"F3.imprint","IMPRINT",EDGE,{"disambiguationData":[TD([[makeQuery(id+"F3.imprint","INTERSECT",VERTEX,{"derivedFrom":[sQuery(id+"F3.wireOp",EDGE,"E50"),subQ0]}),1.0]])],"derivedFrom":subQ0})])],"isStart":false});}
            var Q46;
            {var subQ0=sQuery(id+"F3.wireOp",EDGE,"E52");Q46=makeQuery(id+"F4.opExtrude","CAP_EDGE",EDGE,{"disambiguationData":[OSD([subQ0]),TDD([makeQuery(id+"F3.imprint","IMPRINT",EDGE,{"disambiguationData":[TD([[makeQuery(id+"F3.imprint","INTERSECT",VERTEX,{"derivedFrom":[sQuery(id+"F3.wireOp",EDGE,"E11"),subQ0]}),1.0]])],"derivedFrom":subQ0})])],"isStart":false});}
            var Q47;
            Q47=makeQuery(id+"F4.opExtrude","CAP_FACE",FACE,{"disambiguationData":[OSD([sQuery(id+"F3.wireOp",EDGE,"E11"),sQuery(id+"F3.wireOp",EDGE,"E50"),sQuery(id+"F3.wireOp",EDGE,"E52")])],"isStart":false});
            var Q48;
            {var subQ0=sQuery(id+"F3.wireOp",EDGE,"E58");Q48=makeQuery(id+"F4.opExtrude","CAP_EDGE",EDGE,{"disambiguationData":[OSD([subQ0]),TDD([makeQuery(id+"F3.imprint","IMPRINT",EDGE,{"disambiguationData":[TD([[makeQuery(id+"F3.imprint","INTERSECT",VERTEX,{"derivedFrom":[sQuery(id+"F3.wireOp",EDGE,"E30"),sQuery(id+"F3.wireOp",EDGE,"E39"),subQ0]}),-1.0]])],"derivedFrom":subQ0})])],"isStart":false});}
            var Q49;
            {var subQ0=sQuery(id+"F3.wireOp",EDGE,"E32");Q49=makeQuery(id+"F4.opExtrude","CAP_EDGE",EDGE,{"disambiguationData":[OSD([subQ0]),TDD([makeQuery(id+"F3.imprint","IMPRINT",EDGE,{"disambiguationData":[TD([[makeQuery(id+"F3.imprint","INTERSECT",VERTEX,{"derivedFrom":[sQuery(id+"F3.wireOp",EDGE,"E21"),subQ0,sQuery(id+"F3.wireOp",EDGE,"E39")]}),-1.0]])],"derivedFrom":subQ0})])],"isStart":false});}
            var Q50;
            {var subQ0=sQuery(id+"F3.wireOp",EDGE,"E39");Q50=makeQuery(id+"F4.opExtrude","CAP_EDGE",EDGE,{"disambiguationData":[OSD([subQ0]),TDD([makeQuery(id+"F3.imprint","IMPRINT",EDGE,{"disambiguationData":[TD([[makeQuery(id+"F3.imprint","INTERSECT",VERTEX,{"derivedFrom":[sQuery(id+"F3.wireOp",EDGE,"E21"),sQuery(id+"F3.wireOp",EDGE,"E32"),subQ0]}),1.0]])],"derivedFrom":subQ0})])],"isStart":false});}
            var Q51;
            {var subQ0=sQuery(id+"F3.wireOp",EDGE,"E20");Q51=makeQuery(id+"F4.opExtrude","CAP_EDGE",EDGE,{"disambiguationData":[OSD([subQ0]),TDD([makeQuery(id+"F3.imprint","IMPRINT",EDGE,{"disambiguationData":[TD([[makeQuery(id+"F3.imprint","INTERSECT",VERTEX,{"derivedFrom":[subQ0,sQuery(id+"F3.wireOp",EDGE,"E34"),sQuery(id+"F3.wireOp",EDGE,"E37")]}),-1.0]])],"derivedFrom":subQ0})])],"isStart":false});}
            var Q52;
            {var subQ0=sQuery(id+"F3.wireOp",EDGE,"E38");Q52=makeQuery(id+"F4.opExtrude","CAP_EDGE",EDGE,{"disambiguationData":[OSD([subQ0]),TDD([makeQuery(id+"F3.imprint","IMPRINT",EDGE,{"disambiguationData":[TD([[makeQuery(id+"F3.imprint","INTERSECT",VERTEX,{"derivedFrom":[sQuery(id+"F3.wireOp",EDGE,"E34"),subQ0,sQuery(id+"F3.wireOp",EDGE,"E56")]}),-1.0]])],"derivedFrom":subQ0})])],"isStart":false});}
            var Q53;
            {var subQ0=sQuery(id+"F3.wireOp",EDGE,"E34");Q53=makeQuery(id+"F4.opExtrude","CAP_EDGE",EDGE,{"disambiguationData":[OSD([subQ0]),TDD([makeQuery(id+"F3.imprint","IMPRINT",EDGE,{"disambiguationData":[TD([[makeQuery(id+"F3.imprint","INTERSECT",VERTEX,{"derivedFrom":[sQuery(id+"F3.wireOp",EDGE,"E20"),subQ0,sQuery(id+"F3.wireOp",EDGE,"E37")]}),1.0]])],"derivedFrom":subQ0})])],"isStart":false});}
            chamfer(context, id + "F7", {"entities" : qUnion([Q0, Q1, Q2, Q3, Q4, Q5, Q6, Q7, Q8, Q9, Q10, Q11, Q12, Q13, Q14, Q15, Q16, Q17, Q18, Q19, Q20, Q21, Q22, Q23, Q24, Q25, Q26, Q27, Q28, Q29, Q30, Q31, Q32, Q33, Q34, Q35, Q36, Q37, Q38, Q39, Q40, Q41, Q42, Q43, Q44, Q45, Q46, Q47, Q48, Q49, Q50, Q51, Q52, Q53]), "chamferType" : ChamferType.OFFSET_ANGLE, "width" : 3 * mm, "oppositeDirection" : false, "angle" : 59 * degree, "tangentPropagation" : true});
        }
        {
            var Q0;
            {var subQ0=sQuery(id+"F3.wireOp",EDGE,"E39");Q0=makeQuery(id+"F4.opExtrude","CAP_EDGE",EDGE,{"disambiguationData":[OSD([subQ0]),TDD([makeQuery(id+"F3.imprint","IMPRINT",EDGE,{"disambiguationData":[TD([[makeQuery(id+"F3.imprint","INTERSECT",VERTEX,{"derivedFrom":[sQuery(id+"F3.wireOp",EDGE,"E11"),sQuery(id+"F3.wireOp",EDGE,"E35"),subQ0]}),-1.0]])],"derivedFrom":subQ0})])],"isStart":false});}
            var Q1;
            {var subQ0=sQuery(id+"F3.wireOp",EDGE,"E30");Q1=makeQuery(id+"F4.opExtrude","CAP_EDGE",EDGE,{"disambiguationData":[OSD([subQ0]),TDD([makeQuery(id+"F3.imprint","IMPRINT",EDGE,{"disambiguationData":[TD([[makeQuery(id+"F3.imprint","INTERSECT",VERTEX,{"derivedFrom":[sQuery(id+"F3.wireOp",EDGE,"E11"),subQ0,sQuery(id+"F3.wireOp",EDGE,"E40")]}),1.0]])],"derivedFrom":subQ0})])],"isStart":false});}
            var Q2;
            Q2=makeQuery(id+"F4.opExtrude","CAP_FACE",FACE,{"disambiguationData":[OSD([sQuery(id+"F3.wireOp",EDGE,"E11"),sQuery(id+"F3.wireOp",EDGE,"E30"),sQuery(id+"F3.wireOp",EDGE,"E39")])],"isStart":false});
            var Q3;
            {var subQ0=sQuery(id+"F3.wireOp",EDGE,"E40");Q3=makeQuery(id+"F4.opExtrude","CAP_EDGE",EDGE,{"disambiguationData":[OSD([subQ0]),TDD([makeQuery(id+"F3.imprint","IMPRINT",EDGE,{"disambiguationData":[TD([[makeQuery(id+"F3.imprint","INTERSECT",VERTEX,{"derivedFrom":[sQuery(id+"F3.wireOp",EDGE,"E11"),sQuery(id+"F3.wireOp",EDGE,"E30"),subQ0]}),-1.0]])],"derivedFrom":subQ0})])],"isStart":false});}
            var Q4;
            Q4=makeQuery(id+"F4.opExtrude","CAP_FACE",FACE,{"disambiguationData":[OSD([sQuery(id+"F3.wireOp",EDGE,"E11"),sQuery(id+"F3.wireOp",EDGE,"E32"),sQuery(id+"F3.wireOp",EDGE,"E40")])],"isStart":false});
            var Q5;
            {var subQ0=sQuery(id+"F3.wireOp",EDGE,"E39");Q5=makeQuery(id+"F4.opExtrude","CAP_EDGE",EDGE,{"disambiguationData":[OSD([subQ0]),TDD([makeQuery(id+"F3.imprint","IMPRINT",EDGE,{"disambiguationData":[TD([[makeQuery(id+"F3.imprint","INTERSECT",VERTEX,{"derivedFrom":[sQuery(id+"F3.wireOp",EDGE,"E21"),sQuery(id+"F3.wireOp",EDGE,"E32"),subQ0]}),-1.0]])],"derivedFrom":subQ0})])],"isStart":false});}
            var Q6;
            {var subQ0=sQuery(id+"F3.wireOp",EDGE,"E37");Q6=makeQuery(id+"F4.opExtrude","CAP_EDGE",EDGE,{"disambiguationData":[OSD([subQ0]),TDD([makeQuery(id+"F3.imprint","IMPRINT",EDGE,{"disambiguationData":[TD([[makeQuery(id+"F3.imprint","INTERSECT",VERTEX,{"derivedFrom":[sQuery(id+"F3.wireOp",EDGE,"E21"),subQ0,sQuery(id+"F3.wireOp",EDGE,"E40")]}),1.0]])],"derivedFrom":subQ0})])],"isStart":false});}
            var Q7;
            {var subQ0=sQuery(id+"F3.wireOp",EDGE,"E21");Q7=makeQuery(id+"F4.opExtrude","CAP_EDGE",EDGE,{"disambiguationData":[OSD([subQ0]),TDD([makeQuery(id+"F3.imprint","IMPRINT",EDGE,{"disambiguationData":[TD([[makeQuery(id+"F3.imprint","INTERSECT",VERTEX,{"derivedFrom":[subQ0,sQuery(id+"F3.wireOp",EDGE,"E32"),sQuery(id+"F3.wireOp",EDGE,"E39")]}),-1.0]])],"derivedFrom":subQ0})])],"isStart":false});}
            var Q8;
            {var subQ0=sQuery(id+"F3.wireOp",EDGE,"E40");Q8=makeQuery(id+"F4.opExtrude","CAP_EDGE",EDGE,{"disambiguationData":[OSD([subQ0]),TDD([makeQuery(id+"F3.imprint","IMPRINT",EDGE,{"disambiguationData":[TD([[makeQuery(id+"F3.imprint","INTERSECT",VERTEX,{"derivedFrom":[sQuery(id+"F3.wireOp",EDGE,"E21"),sQuery(id+"F3.wireOp",EDGE,"E37"),subQ0]}),1.0]])],"derivedFrom":subQ0})])],"isStart":false});}
            var Q9;
            {var subQ0=sQuery(id+"F3.wireOp",EDGE,"E37");Q9=makeQuery(id+"F4.opExtrude","CAP_EDGE",EDGE,{"disambiguationData":[OSD([subQ0]),TDD([makeQuery(id+"F3.imprint","IMPRINT",EDGE,{"disambiguationData":[TD([[makeQuery(id+"F3.imprint","INTERSECT",VERTEX,{"derivedFrom":[subQ0,sQuery(id+"F3.wireOp",EDGE,"E58")]}),1.0]])],"derivedFrom":subQ0})])],"isStart":false});}
            var Q10;
            {var subQ0=sQuery(id+"F3.wireOp",EDGE,"E58");Q10=makeQuery(id+"F4.opExtrude","CAP_EDGE",EDGE,{"disambiguationData":[OSD([subQ0]),TDD([makeQuery(id+"F3.imprint","IMPRINT",EDGE,{"disambiguationData":[TD([[makeQuery(id+"F3.imprint","INTERSECT",VERTEX,{"derivedFrom":[sQuery(id+"F3.wireOp",EDGE,"E37"),subQ0]}),1.0]])],"derivedFrom":subQ0})])],"isStart":false});}
            var Q11;
            {var subQ0=sQuery(id+"F3.wireOp",EDGE,"E40");Q11=makeQuery(id+"F4.opExtrude","CAP_EDGE",EDGE,{"disambiguationData":[OSD([subQ0]),TDD([makeQuery(id+"F3.imprint","IMPRINT",EDGE,{"disambiguationData":[TD([[makeQuery(id+"F3.imprint","INTERSECT",VERTEX,{"derivedFrom":[subQ0,sQuery(id+"F3.wireOp",EDGE,"E54")]}),1.0]])],"derivedFrom":subQ0})])],"isStart":false});}
            var Q12;
            {var subQ0=sQuery(id+"F3.wireOp",EDGE,"E47");Q12=makeQuery(id+"F4.opExtrude","CAP_EDGE",EDGE,{"disambiguationData":[OSD([subQ0]),TDD([makeQuery(id+"F3.imprint","IMPRINT",EDGE,{"disambiguationData":[TD([[makeQuery(id+"F3.imprint","INTERSECT",VERTEX,{"derivedFrom":[subQ0,sQuery(id+"F3.wireOp",EDGE,"E54")]}),-1.0]])],"derivedFrom":subQ0})])],"isStart":false});}
            var Q13;
            {var subQ0=sQuery(id+"F3.wireOp",EDGE,"E21");Q13=makeQuery(id+"F4.opExtrude","CAP_EDGE",EDGE,{"disambiguationData":[OSD([subQ0]),TDD([makeQuery(id+"F3.imprint","IMPRINT",EDGE,{"disambiguationData":[TD([[makeQuery(id+"F3.imprint","INTERSECT",VERTEX,{"derivedFrom":[subQ0,sQuery(id+"F3.wireOp",EDGE,"E37"),sQuery(id+"F3.wireOp",EDGE,"E40")]}),-1.0]])],"derivedFrom":subQ0})])],"isStart":false});}
            var Q14;
            {var subQ0=sQuery(id+"F3.wireOp",EDGE,"E39");Q14=makeQuery(id+"F4.opExtrude","CAP_EDGE",EDGE,{"disambiguationData":[OSD([subQ0]),TDD([makeQuery(id+"F3.imprint","IMPRINT",EDGE,{"disambiguationData":[TD([[makeQuery(id+"F3.imprint","INTERSECT",VERTEX,{"derivedFrom":[sQuery(id+"F3.wireOp",EDGE,"E37"),subQ0,sQuery(id+"F3.wireOp",EDGE,"E54")]}),-1.0]])],"derivedFrom":subQ0})])],"isStart":false});}
            var Q15;
            Q15=makeQuery(id+"F4.opExtrude","CAP_FACE",FACE,{"disambiguationData":[OSD([sQuery(id+"F3.wireOp",EDGE,"E39"),sQuery(id+"F3.wireOp",EDGE,"E40"),sQuery(id+"F3.wireOp",EDGE,"E47"),sQuery(id+"F3.wireOp",EDGE,"E54")])],"isStart":false});
            chamfer(context, id + "F8", {"entities" : qUnion([Q0, Q1, Q2, Q3, Q4, Q5, Q6, Q7, Q8, Q9, Q10, Q11, Q12, Q13, Q14, Q15]), "chamferType" : ChamferType.OFFSET_ANGLE, "width" : 3 * mm, "oppositeDirection" : true, "angle" : 59 * degree, "tangentPropagation" : true});
        }
        {
            var Q0;
            {var subQ0=sQuery(id+"F3.wireOp",EDGE,"E41");Q0=makeQuery(id+"F4.opExtrude","CAP_EDGE",EDGE,{"disambiguationData":[OSD([subQ0]),TDD([makeQuery(id+"F3.imprint","IMPRINT",EDGE,{"disambiguationData":[TD([[makeQuery(id+"F3.imprint","INTERSECT",VERTEX,{"derivedFrom":[sQuery(id+"F3.wireOp",EDGE,"E37"),subQ0]}),-1.0]])],"derivedFrom":subQ0})])],"isStart":false});}
            var Q1;
            {var subQ0=sQuery(id+"F3.wireOp",EDGE,"E11");Q1=makeQuery(id+"F4.opExtrude","CAP_EDGE",EDGE,{"disambiguationData":[OSD([subQ0]),TDD([makeQuery(id+"F3.imprint","IMPRINT",EDGE,{"disambiguationData":[TD([[makeQuery(id+"F3.imprint","INTERSECT",VERTEX,{"derivedFrom":[subQ0,sQuery(id+"F3.wireOp",EDGE,"E37")]}),1.0]])],"derivedFrom":subQ0})])],"isStart":false});}
            var Q2;
            {var subQ0=sQuery(id+"F3.wireOp",EDGE,"E37");Q2=makeQuery(id+"F4.opExtrude","CAP_EDGE",EDGE,{"disambiguationData":[OSD([subQ0]),TDD([makeQuery(id+"F3.imprint","IMPRINT",EDGE,{"disambiguationData":[TD([[makeQuery(id+"F3.imprint","INTERSECT",VERTEX,{"derivedFrom":[sQuery(id+"F3.wireOp",EDGE,"E11"),subQ0]}),1.0]])],"derivedFrom":subQ0})])],"isStart":false});}
            var Q3;
            {var subQ0=sQuery(id+"F3.wireOp",EDGE,"E41");Q3=makeQuery(id+"F4.opExtrude","CAP_EDGE",EDGE,{"disambiguationData":[OSD([subQ0]),TDD([makeQuery(id+"F3.imprint","IMPRINT",EDGE,{"disambiguationData":[TD([[makeQuery(id+"F3.imprint","INTERSECT",VERTEX,{"derivedFrom":[subQ0,sQuery(id+"F3.wireOp",EDGE,"E58")]}),1.0]])],"derivedFrom":subQ0})])],"isStart":false});}
            var Q4;
            {var subQ0=sQuery(id+"F3.wireOp",EDGE,"E58");Q4=makeQuery(id+"F4.opExtrude","CAP_EDGE",EDGE,{"disambiguationData":[OSD([subQ0]),TDD([makeQuery(id+"F3.imprint","IMPRINT",EDGE,{"disambiguationData":[TD([[makeQuery(id+"F3.imprint","INTERSECT",VERTEX,{"derivedFrom":[sQuery(id+"F3.wireOp",EDGE,"E41"),subQ0]}),-1.0]])],"derivedFrom":subQ0})])],"isStart":false});}
            var Q5;
            {var subQ0=sQuery(id+"F3.wireOp",EDGE,"E47");Q5=makeQuery(id+"F4.opExtrude","CAP_EDGE",EDGE,{"disambiguationData":[OSD([subQ0]),TDD([makeQuery(id+"F3.imprint","IMPRINT",EDGE,{"disambiguationData":[TD([[makeQuery(id+"F3.imprint","INTERSECT",VERTEX,{"derivedFrom":[subQ0,sQuery(id+"F3.wireOp",EDGE,"E58")]}),1.0]])],"derivedFrom":subQ0})])],"isStart":false});}
            var Q6;
            Q6=makeQuery(id+"F4.opExtrude","CAP_FACE",FACE,{"disambiguationData":[OSD([sQuery(id+"F3.wireOp",EDGE,"E11"),sQuery(id+"F3.wireOp",EDGE,"E47"),sQuery(id+"F3.wireOp",EDGE,"E51")])],"isStart":false});
            var Q7;
            Q7=makeQuery(id+"F4.opExtrude","CAP_FACE",FACE,{"disambiguationData":[OSD([sQuery(id+"F3.wireOp",EDGE,"E21"),sQuery(id+"F3.wireOp",EDGE,"E41"),sQuery(id+"F3.wireOp",EDGE,"E50")])],"isStart":false});
            var Q8;
            Q8=makeQuery(id+"F4.opExtrude","CAP_FACE",FACE,{"disambiguationData":[OSD([sQuery(id+"F3.wireOp",EDGE,"E20"),sQuery(id+"F3.wireOp",EDGE,"E40"),sQuery(id+"F3.wireOp",EDGE,"E44"),sQuery(id+"F3.wireOp",EDGE,"E49"),sQuery(id+"F3.wireOp",EDGE,"E56")])],"isStart":false});
            chamfer(context, id + "F9", {"entities" : qUnion([Q0, Q1, Q2, Q3, Q4, Q5, Q6, Q7, Q8]), "chamferType" : ChamferType.OFFSET_ANGLE, "width" : 3 * mm, "oppositeDirection" : false, "angle" : 59 * degree, "tangentPropagation" : true});
        }
        {
            var Q0;
            {var subQ1=sQuery(id+"F3.wireOp",EDGE,"E10");var subQ3=sQuery(id+"F3.wireOp",EDGE,"E54");var subQ4=makeQuery(id+"F3.imprint","INTERSECT",VERTEX,{"derivedFrom":[subQ1,subQ3]});Q0=makeQuery(id+"F3.imprint","IMPRINT",FACE,{"disambiguationData":[TD([[makeQuery(id+"F3.imprint","IMPRINT",EDGE,{"disambiguationData":[TD([[subQ4,-1.0]])],"derivedFrom":subQ3}),1.0]])]});}
            var Q1;
            {var subQ1=sQuery(id+"F3.wireOp",EDGE,"E10");var subQ3=sQuery(id+"F3.wireOp",EDGE,"E58");var subQ4=makeQuery(id+"F3.imprint","INTERSECT",VERTEX,{"derivedFrom":[subQ1,subQ3]});Q1=makeQuery(id+"F3.imprint","IMPRINT",FACE,{"disambiguationData":[TD([[makeQuery(id+"F3.imprint","IMPRINT",EDGE,{"disambiguationData":[TD([[subQ4,1.0]])],"derivedFrom":subQ1}),1.0]])]});}
            var Q2;
            {var subQ1=sQuery(id+"F3.wireOp",EDGE,"E10");var subQ3=sQuery(id+"F3.wireOp",EDGE,"E56");var subQ4=makeQuery(id+"F3.imprint","INTERSECT",VERTEX,{"derivedFrom":[subQ1,subQ3]});Q2=makeQuery(id+"F3.imprint","IMPRINT",FACE,{"disambiguationData":[TD([[makeQuery(id+"F3.imprint","IMPRINT",EDGE,{"disambiguationData":[TD([[subQ4,-1.0]])],"derivedFrom":subQ1}),1.0]])]});}
            var Q3;
            {var subQ1=sQuery(id+"F3.wireOp",EDGE,"E10");var subQ3=sQuery(id+"F3.wireOp",EDGE,"E56");var subQ4=makeQuery(id+"F3.imprint","INTERSECT",VERTEX,{"derivedFrom":[subQ1,subQ3]});Q3=makeQuery(id+"F3.imprint","IMPRINT",FACE,{"disambiguationData":[TD([[makeQuery(id+"F3.imprint","IMPRINT",EDGE,{"disambiguationData":[TD([[subQ4,-1.0]])],"derivedFrom":subQ3}),1.0]])]});}
            extrude(context, id + "F10", {"entities" : qUnion([Q0, Q1, Q2, Q3]), "depth" : 3 * mm});
        }
        {
            var Q0;
            {var subQ0=sQuery(id+"F3.wireOp",EDGE,"E35");Q0=makeQuery(id+"F4.opExtrude","CAP_EDGE",EDGE,{"disambiguationData":[OSD([subQ0]),TDD([makeQuery(id+"F3.imprint","IMPRINT",EDGE,{"disambiguationData":[TD([[makeQuery(id+"F3.imprint","INTERSECT",VERTEX,{"derivedFrom":[sQuery(id+"F3.wireOp",EDGE,"E28"),subQ0,sQuery(id+"F3.wireOp",EDGE,"E54")]}),1.0]])],"derivedFrom":subQ0})])],"isStart":false});}
            var Q1;
            Q1=makeQuery(id+"F10.opExtrude","CAP_EDGE",EDGE,{"disambiguationData":[OSD([sQuery(id+"F3.wireOp",EDGE,"E28")])],"isStart":false});
            var Q2;
            {var subQ0=sQuery(id+"F3.wireOp",EDGE,"E36");Q2=makeQuery(id+"F4.opExtrude","CAP_EDGE",EDGE,{"disambiguationData":[OSD([subQ0]),TDD([makeQuery(id+"F3.imprint","IMPRINT",EDGE,{"disambiguationData":[TD([[makeQuery(id+"F3.imprint","INTERSECT",VERTEX,{"derivedFrom":[sQuery(id+"F3.wireOp",EDGE,"E33"),subQ0,sQuery(id+"F3.wireOp",EDGE,"E58")]}),1.0]])],"derivedFrom":subQ0})])],"isStart":false});}
            var Q3;
            Q3=makeQuery(id+"F10.opExtrude","CAP_EDGE",EDGE,{"disambiguationData":[OSD([sQuery(id+"F3.wireOp",EDGE,"E33")])],"isStart":false});
            var Q4;
            Q4=makeQuery(id+"F10.opExtrude","CAP_EDGE",EDGE,{"disambiguationData":[OSD([sQuery(id+"F3.wireOp",EDGE,"E30")])],"isStart":false});
            chamfer(context, id + "F11", {"entities" : qUnion([Q0, Q1, Q2, Q3, Q4]), "chamferType" : ChamferType.OFFSET_ANGLE, "width" : 8 * mm, "oppositeDirection" : false, "angle" : 20 * degree, "tangentPropagation" : true});
        }
        {
            var Q0;
            Q0=makeQuery(id+"F10.opExtrude","CAP_EDGE",EDGE,{"disambiguationData":[OSD([sQuery(id+"F3.wireOp",EDGE,"E29")])],"isStart":false});
            chamfer(context, id + "F12", {"entities" : qUnion([Q0]), "chamferType" : ChamferType.OFFSET_ANGLE, "width" : 8 * mm, "oppositeDirection" : true, "angle" : 20 * degree, "tangentPropagation" : true});
        }
        {
            var Q0;
            {var subQ0=sQuery(id+"F3.wireOp",EDGE,"E32");var subQ1=sQuery(id+"F3.wireOp",EDGE,"E29");var subQ2=makeQuery(id+"F3.imprint","INTERSECT",VERTEX,{"derivedFrom":[sQuery(id+"F3.wireOp",EDGE,"E13"),subQ1,subQ0]});Q0=makeQuery(id+"F3.imprint","IMPRINT",FACE,{"disambiguationData":[TD([[makeQuery(id+"F3.imprint","IMPRINT",EDGE,{"disambiguationData":[TD([[subQ2,1.0]])],"derivedFrom":subQ1}),1.0]])]});}
            var Q1;
            {var subQ0=sQuery(id+"F3.wireOp",EDGE,"E37");var subQ1=sQuery(id+"F3.wireOp",EDGE,"E31");var subQ2=makeQuery(id+"F3.imprint","INTERSECT",VERTEX,{"derivedFrom":[sQuery(id+"F3.wireOp",EDGE,"E13"),subQ1,subQ0]});Q1=makeQuery(id+"F3.imprint","IMPRINT",FACE,{"disambiguationData":[TD([[makeQuery(id+"F3.imprint","IMPRINT",EDGE,{"disambiguationData":[TD([[subQ2,1.0]])],"derivedFrom":subQ1}),1.0]])]});}
            var Q2;
            {var subQ0=sQuery(id+"F3.wireOp",EDGE,"E38");var subQ1=sQuery(id+"F3.wireOp",EDGE,"E33");var subQ2=makeQuery(id+"F3.imprint","INTERSECT",VERTEX,{"derivedFrom":[sQuery(id+"F3.wireOp",EDGE,"E13"),subQ1,subQ0]});Q2=makeQuery(id+"F3.imprint","IMPRINT",FACE,{"disambiguationData":[TD([[makeQuery(id+"F3.imprint","IMPRINT",EDGE,{"disambiguationData":[TD([[subQ2,-1.0]])],"derivedFrom":subQ1}),-1.0]])]});}
            var Q3;
            {var subQ0=sQuery(id+"F3.wireOp",EDGE,"E43");var subQ1=sQuery(id+"F3.wireOp",EDGE,"E34");var subQ2=makeQuery(id+"F3.imprint","INTERSECT",VERTEX,{"derivedFrom":[sQuery(id+"F3.wireOp",EDGE,"E13"),subQ1,subQ0]});Q3=makeQuery(id+"F3.imprint","IMPRINT",FACE,{"disambiguationData":[TD([[makeQuery(id+"F3.imprint","IMPRINT",EDGE,{"disambiguationData":[TD([[subQ2,-1.0]])],"derivedFrom":subQ1}),-1.0]])]});}
            var Q4;
            {var subQ0=sQuery(id+"F3.wireOp",EDGE,"E56");var subQ1=sQuery(id+"F3.wireOp",EDGE,"E40");var subQ2=makeQuery(id+"F3.imprint","INTERSECT",VERTEX,{"derivedFrom":[subQ1,subQ0]});Q4=makeQuery(id+"F3.imprint","IMPRINT",FACE,{"disambiguationData":[TD([[makeQuery(id+"F3.imprint","IMPRINT",EDGE,{"disambiguationData":[TD([[subQ2,-1.0]])],"derivedFrom":subQ1}),-1.0]])]});}
            var Q5;
            {var subQ1=sQuery(id+"F3.wireOp",EDGE,"E40");var subQ3=sQuery(id+"F3.wireOp",EDGE,"E44");var subQ4=makeQuery(id+"F3.imprint","INTERSECT",VERTEX,{"derivedFrom":[subQ1,subQ3]});Q5=makeQuery(id+"F3.imprint","IMPRINT",FACE,{"disambiguationData":[TD([[makeQuery(id+"F3.imprint","IMPRINT",EDGE,{"disambiguationData":[TD([[subQ4,-1.0]])],"derivedFrom":subQ3}),-1.0]])]});}
            var Q6;
            {var subQ0=sQuery(id+"F3.wireOp",EDGE,"E35");var subQ3=sQuery(id+"F3.wireOp",EDGE,"E28");var subQ5=makeQuery(id+"F3.imprint","INTERSECT",VERTEX,{"derivedFrom":[subQ3,subQ0,sQuery(id+"F3.wireOp",EDGE,"E54")]});Q6=makeQuery(id+"F3.imprint","IMPRINT",FACE,{"disambiguationData":[TD([[makeQuery(id+"F3.imprint","IMPRINT",EDGE,{"disambiguationData":[TD([[subQ5,1.0]])],"derivedFrom":subQ3}),1.0]])]});}
            var Q7;
            {var subQ1=sQuery(id+"F3.wireOp",EDGE,"E20");var subQ3=sQuery(id+"F3.wireOp",EDGE,"E33");var subQ4=makeQuery(id+"F3.imprint","INTERSECT",VERTEX,{"derivedFrom":[subQ1,sQuery(id+"F3.wireOp",EDGE,"E32"),subQ3]});Q7=makeQuery(id+"F3.imprint","IMPRINT",FACE,{"disambiguationData":[TD([[makeQuery(id+"F3.imprint","IMPRINT",EDGE,{"disambiguationData":[TD([[subQ4,-1.0]])],"derivedFrom":subQ3}),1.0]])]});}
            var Q8;
            {var subQ0=sQuery(id+"F3.wireOp",EDGE,"E32");var subQ1=sQuery(id+"F3.wireOp",EDGE,"E20");var subQ2=makeQuery(id+"F3.imprint","INTERSECT",VERTEX,{"derivedFrom":[subQ1,subQ0,sQuery(id+"F3.wireOp",EDGE,"E33")]});Q8=makeQuery(id+"F3.imprint","IMPRINT",FACE,{"disambiguationData":[TD([[makeQuery(id+"F3.imprint","IMPRINT",EDGE,{"disambiguationData":[TD([[subQ2,-1.0]])],"derivedFrom":subQ1}),1.0]])]});}
            var Q9;
            {var subQ1=sQuery(id+"F3.wireOp",EDGE,"E20");var subQ3=sQuery(id+"F3.wireOp",EDGE,"E37");var subQ4=makeQuery(id+"F3.imprint","INTERSECT",VERTEX,{"derivedFrom":[subQ1,sQuery(id+"F3.wireOp",EDGE,"E34"),subQ3]});Q9=makeQuery(id+"F3.imprint","IMPRINT",FACE,{"disambiguationData":[TD([[makeQuery(id+"F3.imprint","IMPRINT",EDGE,{"disambiguationData":[TD([[subQ4,-1.0]])],"derivedFrom":subQ3}),-1.0]])]});}
            var Q10;
            {var subQ0=sQuery(id+"F3.wireOp",EDGE,"E47");var subQ3=sQuery(id+"F3.wireOp",EDGE,"E40");var subQ5=makeQuery(id+"F3.imprint","INTERSECT",VERTEX,{"derivedFrom":[subQ3,subQ0]});Q10=makeQuery(id+"F3.imprint","IMPRINT",FACE,{"disambiguationData":[TD([[makeQuery(id+"F3.imprint","IMPRINT",EDGE,{"disambiguationData":[TD([[subQ5,-1.0]])],"derivedFrom":subQ3}),-1.0]])]});}
            var Q11;
            {var subQ0=sQuery(id+"F3.wireOp",EDGE,"E50");var subQ1=sQuery(id+"F3.wireOp",EDGE,"E49");var subQ2=makeQuery(id+"F3.imprint","INTERSECT",VERTEX,{"derivedFrom":[subQ1,subQ0]});Q11=makeQuery(id+"F3.imprint","IMPRINT",FACE,{"disambiguationData":[TD([[makeQuery(id+"F3.imprint","IMPRINT",EDGE,{"disambiguationData":[TD([[subQ2,1.0]])],"derivedFrom":subQ1}),-1.0]])]});}
            var Q12;
            {var subQ3=sQuery(id+"F3.wireOp",EDGE,"E44");var subQ5=sQuery(id+"F3.wireOp",EDGE,"E54");var subQ6=makeQuery(id+"F3.imprint","INTERSECT",VERTEX,{"derivedFrom":[subQ3,subQ5]});Q12=makeQuery(id+"F3.imprint","IMPRINT",FACE,{"disambiguationData":[TD([[makeQuery(id+"F3.imprint","IMPRINT",EDGE,{"disambiguationData":[TD([[subQ6,-1.0]])],"derivedFrom":subQ5}),-1.0]])]});}
            var Q13;
            {var subQ0=sQuery(id+"F3.wireOp",EDGE,"E35");var subQ1=sQuery(id+"F3.wireOp",EDGE,"E33");var subQ2=makeQuery(id+"F3.imprint","INTERSECT",VERTEX,{"derivedFrom":[sQuery(id+"F3.wireOp",EDGE,"E21"),subQ1,subQ0]});Q13=makeQuery(id+"F3.imprint","IMPRINT",FACE,{"disambiguationData":[TD([[makeQuery(id+"F3.imprint","IMPRINT",EDGE,{"disambiguationData":[TD([[subQ2,1.0]])],"derivedFrom":subQ1}),1.0]])]});}
            var Q14;
            {var subQ0=sQuery(id+"F3.wireOp",EDGE,"E34");var subQ1=sQuery(id+"F3.wireOp",EDGE,"E30");var subQ2=makeQuery(id+"F3.imprint","INTERSECT",VERTEX,{"derivedFrom":[sQuery(id+"F3.wireOp",EDGE,"E21"),subQ1,subQ0]});Q14=makeQuery(id+"F3.imprint","IMPRINT",FACE,{"disambiguationData":[TD([[makeQuery(id+"F3.imprint","IMPRINT",EDGE,{"disambiguationData":[TD([[subQ2,1.0]])],"derivedFrom":subQ1}),-1.0]])]});}
            var Q15;
            {var subQ0=sQuery(id+"F3.wireOp",EDGE,"E39");var subQ1=sQuery(id+"F3.wireOp",EDGE,"E32");var subQ2=makeQuery(id+"F3.imprint","INTERSECT",VERTEX,{"derivedFrom":[sQuery(id+"F3.wireOp",EDGE,"E21"),subQ1,subQ0]});Q15=makeQuery(id+"F3.imprint","IMPRINT",FACE,{"disambiguationData":[TD([[makeQuery(id+"F3.imprint","IMPRINT",EDGE,{"disambiguationData":[TD([[subQ2,1.0]])],"derivedFrom":subQ1}),-1.0]])]});}
            var Q16;
            {var subQ0=sQuery(id+"F3.wireOp",EDGE,"E40");var subQ3=sQuery(id+"F3.wireOp",EDGE,"E54");var subQ5=makeQuery(id+"F3.imprint","INTERSECT",VERTEX,{"derivedFrom":[subQ0,subQ3]});Q16=makeQuery(id+"F3.imprint","IMPRINT",FACE,{"disambiguationData":[TD([[makeQuery(id+"F3.imprint","IMPRINT",EDGE,{"disambiguationData":[TD([[subQ5,1.0]])],"derivedFrom":subQ0}),-1.0]])]});}
            var Q17;
            {var subQ0=sQuery(id+"F3.wireOp",EDGE,"E50");var subQ1=sQuery(id+"F3.wireOp",EDGE,"E41");var subQ2=makeQuery(id+"F3.imprint","INTERSECT",VERTEX,{"derivedFrom":[subQ1,subQ0]});Q17=makeQuery(id+"F3.imprint","IMPRINT",FACE,{"disambiguationData":[TD([[makeQuery(id+"F3.imprint","IMPRINT",EDGE,{"disambiguationData":[TD([[subQ2,-1.0]])],"derivedFrom":subQ0}),-1.0]])]});}
            var Q18;
            {var subQ5=sQuery(id+"F3.wireOp",EDGE,"E54");var subQ6=sQuery(id+"F3.wireOp",EDGE,"E41");var subQ7=makeQuery(id+"F3.imprint","INTERSECT",VERTEX,{"derivedFrom":[subQ6,subQ5]});Q18=makeQuery(id+"F3.imprint","IMPRINT",FACE,{"disambiguationData":[TD([[makeQuery(id+"F3.imprint","IMPRINT",EDGE,{"disambiguationData":[TD([[subQ7,-1.0]])],"derivedFrom":subQ6}),-1.0]])]});}
            var Q19;
            {var subQ0=sQuery(id+"F3.wireOp",EDGE,"E44");var subQ1=sQuery(id+"F3.wireOp",EDGE,"E12");var subQ2=makeQuery(id+"F3.imprint","INTERSECT",VERTEX,{"derivedFrom":[subQ1,subQ0]});Q19=makeQuery(id+"F3.imprint","IMPRINT",FACE,{"disambiguationData":[TD([[makeQuery(id+"F3.imprint","IMPRINT",EDGE,{"disambiguationData":[TD([[subQ2,-1.0]])],"derivedFrom":subQ1}),-1.0]])]});}
            var Q20;
            {var subQ1=sQuery(id+"F3.wireOp",EDGE,"E21");var subQ3=sQuery(id+"F3.wireOp",EDGE,"E33");var subQ4=makeQuery(id+"F3.imprint","INTERSECT",VERTEX,{"derivedFrom":[subQ1,subQ3,sQuery(id+"F3.wireOp",EDGE,"E35")]});Q20=makeQuery(id+"F3.imprint","IMPRINT",FACE,{"disambiguationData":[TD([[makeQuery(id+"F3.imprint","IMPRINT",EDGE,{"disambiguationData":[TD([[subQ4,-1.0]])],"derivedFrom":subQ3}),1.0]])]});}
            var Q21;
            {var subQ0=sQuery(id+"F3.wireOp",EDGE,"E35");var subQ1=sQuery(id+"F3.wireOp",EDGE,"E21");var subQ2=makeQuery(id+"F3.imprint","INTERSECT",VERTEX,{"derivedFrom":[subQ1,sQuery(id+"F3.wireOp",EDGE,"E33"),subQ0]});Q21=makeQuery(id+"F3.imprint","IMPRINT",FACE,{"disambiguationData":[TD([[makeQuery(id+"F3.imprint","IMPRINT",EDGE,{"disambiguationData":[TD([[subQ2,-1.0]])],"derivedFrom":subQ1}),1.0]])]});}
            var Q22;
            {var subQ0=sQuery(id+"F3.wireOp",EDGE,"E30");var subQ1=sQuery(id+"F3.wireOp",EDGE,"E21");var subQ2=makeQuery(id+"F3.imprint","INTERSECT",VERTEX,{"derivedFrom":[subQ1,subQ0,sQuery(id+"F3.wireOp",EDGE,"E34")]});Q22=makeQuery(id+"F3.imprint","IMPRINT",FACE,{"disambiguationData":[TD([[makeQuery(id+"F3.imprint","IMPRINT",EDGE,{"disambiguationData":[TD([[subQ2,-1.0]])],"derivedFrom":subQ1}),1.0]])]});}
            var Q23;
            {var subQ0=sQuery(id+"F3.wireOp",EDGE,"E32");var subQ1=sQuery(id+"F3.wireOp",EDGE,"E21");var subQ2=makeQuery(id+"F3.imprint","INTERSECT",VERTEX,{"derivedFrom":[subQ1,subQ0,sQuery(id+"F3.wireOp",EDGE,"E39")]});Q23=makeQuery(id+"F3.imprint","IMPRINT",FACE,{"disambiguationData":[TD([[makeQuery(id+"F3.imprint","IMPRINT",EDGE,{"disambiguationData":[TD([[subQ2,-1.0]])],"derivedFrom":subQ1}),1.0]])]});}
            var Q24;
            {var subQ0=sQuery(id+"F3.wireOp",EDGE,"E37");var subQ5=sQuery(id+"F3.wireOp",EDGE,"E58");var subQ6=makeQuery(id+"F3.imprint","INTERSECT",VERTEX,{"derivedFrom":[subQ0,subQ5]});Q24=makeQuery(id+"F3.imprint","IMPRINT",FACE,{"disambiguationData":[TD([[makeQuery(id+"F3.imprint","IMPRINT",EDGE,{"disambiguationData":[TD([[subQ6,-1.0]])],"derivedFrom":subQ5}),-1.0]])]});}
            var Q25;
            {var subQ1=sQuery(id+"F3.wireOp",EDGE,"E50");var subQ5=sQuery(id+"F3.wireOp",EDGE,"E21");var subQ6=makeQuery(id+"F3.imprint","INTERSECT",VERTEX,{"derivedFrom":[subQ5,subQ1]});Q25=makeQuery(id+"F3.imprint","IMPRINT",FACE,{"disambiguationData":[TD([[makeQuery(id+"F3.imprint","IMPRINT",EDGE,{"disambiguationData":[TD([[subQ6,1.0]])],"derivedFrom":subQ1}),-1.0]])]});}
            var Q26;
            {var subQ5=sQuery(id+"F3.wireOp",EDGE,"E45");Q26=makeQuery(id+"F3.imprint","IMPRINT",FACE,{"disambiguationData":[TD([[makeQuery(id+"F3.imprint","IMPRINT",EDGE,{"derivedFrom":subQ5}),1.0]])]});}
            var Q27;
            {var subQ0=sQuery(id+"F3.wireOp",EDGE,"E36");var subQ1=sQuery(id+"F3.wireOp",EDGE,"E34");var subQ2=makeQuery(id+"F3.imprint","INTERSECT",VERTEX,{"derivedFrom":[sQuery(id+"F3.wireOp",EDGE,"E11"),subQ1,subQ0]});Q27=makeQuery(id+"F3.imprint","IMPRINT",FACE,{"disambiguationData":[TD([[makeQuery(id+"F3.imprint","IMPRINT",EDGE,{"disambiguationData":[TD([[subQ2,1.0]])],"derivedFrom":subQ1}),1.0]])]});}
            var Q28;
            {var subQ0=sQuery(id+"F3.wireOp",EDGE,"E39");var subQ1=sQuery(id+"F3.wireOp",EDGE,"E35");var subQ2=makeQuery(id+"F3.imprint","INTERSECT",VERTEX,{"derivedFrom":[sQuery(id+"F3.wireOp",EDGE,"E11"),subQ1,subQ0]});Q28=makeQuery(id+"F3.imprint","IMPRINT",FACE,{"disambiguationData":[TD([[makeQuery(id+"F3.imprint","IMPRINT",EDGE,{"disambiguationData":[TD([[subQ2,1.0]])],"derivedFrom":subQ1}),-1.0]])]});}
            var Q29;
            {var subQ0=sQuery(id+"F3.wireOp",EDGE,"E40");var subQ1=sQuery(id+"F3.wireOp",EDGE,"E30");var subQ2=makeQuery(id+"F3.imprint","INTERSECT",VERTEX,{"derivedFrom":[sQuery(id+"F3.wireOp",EDGE,"E11"),subQ1,subQ0]});Q29=makeQuery(id+"F3.imprint","IMPRINT",FACE,{"disambiguationData":[TD([[makeQuery(id+"F3.imprint","IMPRINT",EDGE,{"disambiguationData":[TD([[subQ2,1.0]])],"derivedFrom":subQ1}),-1.0]])]});}
            var Q30;
            {var subQ3=sQuery(id+"F3.wireOp",EDGE,"E58");var subQ5=sQuery(id+"F3.wireOp",EDGE,"E37");var subQ6=makeQuery(id+"F3.imprint","INTERSECT",VERTEX,{"derivedFrom":[subQ5,subQ3]});Q30=makeQuery(id+"F3.imprint","IMPRINT",FACE,{"disambiguationData":[TD([[makeQuery(id+"F3.imprint","IMPRINT",EDGE,{"disambiguationData":[TD([[subQ6,-1.0]])],"derivedFrom":subQ5}),1.0]])]});}
            var Q31;
            {var subQ5=sQuery(id+"F3.wireOp",EDGE,"E11");var subQ8=sQuery(id+"F3.wireOp",EDGE,"E37");var subQ11=makeQuery(id+"F3.imprint","INTERSECT",VERTEX,{"derivedFrom":[subQ5,subQ8]});Q31=makeQuery(id+"F3.imprint","IMPRINT",FACE,{"disambiguationData":[TD([[makeQuery(id+"F3.imprint","IMPRINT",EDGE,{"disambiguationData":[TD([[subQ11,-1.0]])],"derivedFrom":subQ5}),-1.0]])]});}
            var Q32;
            {var subQ1=sQuery(id+"F3.wireOp",EDGE,"E47");var subQ9=sQuery(id+"F3.wireOp",EDGE,"E11");var subQ10=makeQuery(id+"F3.imprint","INTERSECT",VERTEX,{"derivedFrom":[subQ9,subQ1]});Q32=makeQuery(id+"F3.imprint","IMPRINT",FACE,{"disambiguationData":[TD([[makeQuery(id+"F3.imprint","IMPRINT",EDGE,{"disambiguationData":[TD([[subQ10,-1.0]])],"derivedFrom":subQ9}),-1.0]])]});}
            var Q33;
            {var subQ0=sQuery(id+"F3.wireOp",EDGE,"E50");var subQ5=sQuery(id+"F3.wireOp",EDGE,"E52");var subQ6=makeQuery(id+"F3.imprint","INTERSECT",VERTEX,{"derivedFrom":[subQ0,subQ5]});Q33=makeQuery(id+"F3.imprint","IMPRINT",FACE,{"disambiguationData":[TD([[makeQuery(id+"F3.imprint","IMPRINT",EDGE,{"disambiguationData":[TD([[subQ6,1.0]])],"derivedFrom":subQ5}),-1.0]])]});}
            var Q34;
            {var subQ1=sQuery(id+"F3.wireOp",EDGE,"E12");var subQ3=sQuery(id+"F3.wireOp",EDGE,"E56");var subQ4=makeQuery(id+"F3.imprint","INTERSECT",VERTEX,{"derivedFrom":[subQ1,subQ3]});Q34=makeQuery(id+"F3.imprint","IMPRINT",FACE,{"disambiguationData":[TD([[makeQuery(id+"F3.imprint","IMPRINT",EDGE,{"disambiguationData":[TD([[subQ4,1.0]])],"derivedFrom":subQ3}),-1.0]])]});}
            extrude(context, id + "F13", {"entities" : qUnion([Q0, Q1, Q2, Q3, Q4, Q5, Q6, Q7, Q8, Q9, Q10, Q11, Q12, Q13, Q14, Q15, Q16, Q17, Q18, Q19, Q20, Q21, Q22, Q23, Q24, Q25, Q26, Q27, Q28, Q29, Q30, Q31, Q32, Q33, Q34]), "depth" : 3 * mm});
        }
        {
            var Q0;
            Q0=makeQuery(id+"F13.opExtrude","CAP_FACE",FACE,{"disambiguationData":[OSD([sQuery(id+"F3.wireOp",EDGE,"E29"),sQuery(id+"F3.wireOp",EDGE,"E32"),sQuery(id+"F3.wireOp",EDGE,"E56")])],"isStart":false});
            var Q1;
            Q1=makeQuery(id+"F13.opExtrude","CAP_FACE",FACE,{"disambiguationData":[OSD([sQuery(id+"F3.wireOp",EDGE,"E31"),sQuery(id+"F3.wireOp",EDGE,"E37"),sQuery(id+"F3.wireOp",EDGE,"E56")])],"isStart":false});
            var Q2;
            Q2=makeQuery(id+"F13.opExtrude","CAP_FACE",FACE,{"disambiguationData":[OSD([sQuery(id+"F3.wireOp",EDGE,"E20"),sQuery(id+"F3.wireOp",EDGE,"E30"),sQuery(id+"F3.wireOp",EDGE,"E33")])],"isStart":false});
            var Q3;
            Q3=makeQuery(id+"F13.opExtrude","CAP_FACE",FACE,{"disambiguationData":[OSD([sQuery(id+"F3.wireOp",EDGE,"E20"),sQuery(id+"F3.wireOp",EDGE,"E28"),sQuery(id+"F3.wireOp",EDGE,"E35")])],"isStart":false});
            var Q4;
            Q4=makeQuery(id+"F13.opExtrude","CAP_FACE",FACE,{"disambiguationData":[OSD([sQuery(id+"F3.wireOp",EDGE,"E20"),sQuery(id+"F3.wireOp",EDGE,"E32"),sQuery(id+"F3.wireOp",EDGE,"E34")])],"isStart":false});
            var Q5;
            Q5=makeQuery(id+"F13.opExtrude","CAP_FACE",FACE,{"disambiguationData":[OSD([sQuery(id+"F3.wireOp",EDGE,"E20"),sQuery(id+"F3.wireOp",EDGE,"E37"),sQuery(id+"F3.wireOp",EDGE,"E39")])],"isStart":false});
            var Q6;
            Q6=makeQuery(id+"F13.opExtrude","CAP_FACE",FACE,{"disambiguationData":[OSD([sQuery(id+"F3.wireOp",EDGE,"E20"),sQuery(id+"F3.wireOp",EDGE,"E40"),sQuery(id+"F3.wireOp",EDGE,"E47")])],"isStart":false});
            var Q7;
            Q7=makeQuery(id+"F13.opExtrude","CAP_FACE",FACE,{"disambiguationData":[OSD([sQuery(id+"F3.wireOp",EDGE,"E20"),sQuery(id+"F3.wireOp",EDGE,"E41"),sQuery(id+"F3.wireOp",EDGE,"E49"),sQuery(id+"F3.wireOp",EDGE,"E50"),sQuery(id+"F3.wireOp",EDGE,"E54")])],"isStart":false});
            var Q8;
            Q8=makeQuery(id+"F13.opExtrude","CAP_FACE",FACE,{"disambiguationData":[OSD([sQuery(id+"F3.wireOp",EDGE,"E40"),sQuery(id+"F3.wireOp",EDGE,"E44"),sQuery(id+"F3.wireOp",EDGE,"E46"),sQuery(id+"F3.wireOp",EDGE,"E56")])],"isStart":false});
            var Q9;
            Q9=makeQuery(id+"F13.opExtrude","CAP_FACE",FACE,{"disambiguationData":[OSD([sQuery(id+"F3.wireOp",EDGE,"E20"),sQuery(id+"F3.wireOp",EDGE,"E44"),sQuery(id+"F3.wireOp",EDGE,"E48"),sQuery(id+"F3.wireOp",EDGE,"E54")])],"isStart":false});
            var Q10;
            Q10=makeQuery(id+"F13.opExtrude","CAP_FACE",FACE,{"disambiguationData":[OSD([sQuery(id+"F3.wireOp",EDGE,"E33"),sQuery(id+"F3.wireOp",EDGE,"E35"),sQuery(id+"F3.wireOp",EDGE,"E54")])],"isStart":false});
            var Q11;
            Q11=makeQuery(id+"F13.opExtrude","CAP_FACE",FACE,{"disambiguationData":[OSD([sQuery(id+"F3.wireOp",EDGE,"E21"),sQuery(id+"F3.wireOp",EDGE,"E33"),sQuery(id+"F3.wireOp",EDGE,"E36")])],"isStart":false});
            var Q12;
            Q12=makeQuery(id+"F13.opExtrude","CAP_FACE",FACE,{"disambiguationData":[OSD([sQuery(id+"F3.wireOp",EDGE,"E34"),sQuery(id+"F3.wireOp",EDGE,"E36"),sQuery(id+"F3.wireOp",EDGE,"E58")])],"isStart":false});
            var Q13;
            Q13=makeQuery(id+"F13.opExtrude","CAP_FACE",FACE,{"disambiguationData":[OSD([sQuery(id+"F3.wireOp",EDGE,"E21"),sQuery(id+"F3.wireOp",EDGE,"E34"),sQuery(id+"F3.wireOp",EDGE,"E35")])],"isStart":false});
            var Q14;
            Q14=makeQuery(id+"F13.opExtrude","CAP_FACE",FACE,{"disambiguationData":[OSD([sQuery(id+"F3.wireOp",EDGE,"E21"),sQuery(id+"F3.wireOp",EDGE,"E30"),sQuery(id+"F3.wireOp",EDGE,"E39")])],"isStart":false});
            var Q15;
            Q15=makeQuery(id+"F13.opExtrude","CAP_FACE",FACE,{"disambiguationData":[OSD([sQuery(id+"F3.wireOp",EDGE,"E21"),sQuery(id+"F3.wireOp",EDGE,"E32"),sQuery(id+"F3.wireOp",EDGE,"E40")])],"isStart":false});
            var Q16;
            Q16=makeQuery(id+"F13.opExtrude","CAP_FACE",FACE,{"disambiguationData":[OSD([sQuery(id+"F3.wireOp",EDGE,"E21"),sQuery(id+"F3.wireOp",EDGE,"E37"),sQuery(id+"F3.wireOp",EDGE,"E41"),sQuery(id+"F3.wireOp",EDGE,"E58")])],"isStart":false});
            var Q17;
            Q17=makeQuery(id+"F13.opExtrude","CAP_FACE",FACE,{"disambiguationData":[OSD([sQuery(id+"F3.wireOp",EDGE,"E41"),sQuery(id+"F3.wireOp",EDGE,"E47"),sQuery(id+"F3.wireOp",EDGE,"E50"),sQuery(id+"F3.wireOp",EDGE,"E54")])],"isStart":false});
            var Q18;
            Q18=makeQuery(id+"F13.opExtrude","CAP_FACE",FACE,{"disambiguationData":[OSD([sQuery(id+"F3.wireOp",EDGE,"E21"),sQuery(id+"F3.wireOp",EDGE,"E47"),sQuery(id+"F3.wireOp",EDGE,"E50"),sQuery(id+"F3.wireOp",EDGE,"E51"),sQuery(id+"F3.wireOp",EDGE,"E58")])],"isStart":false});
            var Q19;
            Q19=makeQuery(id+"F13.opExtrude","CAP_FACE",FACE,{"disambiguationData":[OSD([sQuery(id+"F3.wireOp",EDGE,"E21"),sQuery(id+"F3.wireOp",EDGE,"E45"),sQuery(id+"F3.wireOp",EDGE,"E50"),sQuery(id+"F3.wireOp",EDGE,"E52"),sQuery(id+"F3.wireOp",EDGE,"E58")])],"isStart":false});
            chamfer(context, id + "F14", {"entities" : qUnion([Q0, Q1, Q2, Q3, Q4, Q5, Q6, Q7, Q8, Q9, Q10, Q11, Q12, Q13, Q14, Q15, Q16, Q17, Q18, Q19]), "chamferType" : ChamferType.OFFSET_ANGLE, "width" : 3 * mm, "oppositeDirection" : true, "angle" : 59 * degree, "tangentPropagation" : true});
        }
        {
            var Q0;
            Q0=makeQuery(id+"F13.opExtrude","CAP_FACE",FACE,{"disambiguationData":[OSD([sQuery(id+"F3.wireOp",EDGE,"E30"),sQuery(id+"F3.wireOp",EDGE,"E34"),sQuery(id+"F3.wireOp",EDGE,"E54")])],"isStart":false});
            var Q1;
            Q1=makeQuery(id+"F13.opExtrude","CAP_FACE",FACE,{"disambiguationData":[OSD([sQuery(id+"F3.wireOp",EDGE,"E35"),sQuery(id+"F3.wireOp",EDGE,"E39"),sQuery(id+"F3.wireOp",EDGE,"E58")])],"isStart":false});
            var Q2;
            Q2=makeQuery(id+"F13.opExtrude","CAP_FACE",FACE,{"disambiguationData":[OSD([sQuery(id+"F3.wireOp",EDGE,"E30"),sQuery(id+"F3.wireOp",EDGE,"E40"),sQuery(id+"F3.wireOp",EDGE,"E58")])],"isStart":false});
            var Q3;
            Q3=makeQuery(id+"F13.opExtrude","CAP_FACE",FACE,{"disambiguationData":[OSD([sQuery(id+"F3.wireOp",EDGE,"E32"),sQuery(id+"F3.wireOp",EDGE,"E37"),sQuery(id+"F3.wireOp",EDGE,"E41"),sQuery(id+"F3.wireOp",EDGE,"E58")])],"isStart":false});
            var Q4;
            Q4=makeQuery(id+"F13.opExtrude","CAP_FACE",FACE,{"disambiguationData":[OSD([sQuery(id+"F3.wireOp",EDGE,"E32"),sQuery(id+"F3.wireOp",EDGE,"E39"),sQuery(id+"F3.wireOp",EDGE,"E54")])],"isStart":false});
            var Q5;
            Q5=makeQuery(id+"F13.opExtrude","CAP_FACE",FACE,{"disambiguationData":[OSD([sQuery(id+"F3.wireOp",EDGE,"E37"),sQuery(id+"F3.wireOp",EDGE,"E40"),sQuery(id+"F3.wireOp",EDGE,"E54")])],"isStart":false});
            var Q6;
            Q6=makeQuery(id+"F13.opExtrude","CAP_FACE",FACE,{"disambiguationData":[OSD([sQuery(id+"F3.wireOp",EDGE,"E11"),sQuery(id+"F3.wireOp",EDGE,"E37"),sQuery(id+"F3.wireOp",EDGE,"E41"),sQuery(id+"F3.wireOp",EDGE,"E47"),sQuery(id+"F3.wireOp",EDGE,"E51"),sQuery(id+"F3.wireOp",EDGE,"E58")])],"isStart":false});
            var Q7;
            Q7=makeQuery(id+"F13.opExtrude","CAP_FACE",FACE,{"disambiguationData":[OSD([sQuery(id+"F3.wireOp",EDGE,"E11"),sQuery(id+"F3.wireOp",EDGE,"E47"),sQuery(id+"F3.wireOp",EDGE,"E50"),sQuery(id+"F3.wireOp",EDGE,"E51"),sQuery(id+"F3.wireOp",EDGE,"E52"),sQuery(id+"F3.wireOp",EDGE,"E58")])],"isStart":false});
            var Q8;
            Q8=makeQuery(id+"F13.opExtrude","CAP_FACE",FACE,{"disambiguationData":[OSD([sQuery(id+"F3.wireOp",EDGE,"E21"),sQuery(id+"F3.wireOp",EDGE,"E41"),sQuery(id+"F3.wireOp",EDGE,"E44"),sQuery(id+"F3.wireOp",EDGE,"E48"),sQuery(id+"F3.wireOp",EDGE,"E50"),sQuery(id+"F3.wireOp",EDGE,"E54")])],"isStart":false});
            chamfer(context, id + "F15", {"entities" : qUnion([Q0, Q1, Q2, Q3, Q4, Q5, Q6, Q7, Q8]), "chamferType" : ChamferType.OFFSET_ANGLE, "width" : 3 * mm, "oppositeDirection" : false, "angle" : 59 * degree, "tangentPropagation" : true});
        }
        {
            var Q0;
            {var subQ1=sQuery(id+"F3.wireOp",EDGE,"E30");var subQ3=sQuery(id+"F3.wireOp",EDGE,"E56");var subQ4=makeQuery(id+"F3.imprint","INTERSECT",VERTEX,{"derivedFrom":[sQuery(id+"F3.wireOp",EDGE,"E29"),subQ1,subQ3]});Q0=makeQuery(id+"F3.imprint","IMPRINT",FACE,{"disambiguationData":[TD([[makeQuery(id+"F3.imprint","IMPRINT",EDGE,{"disambiguationData":[TD([[subQ4,-1.0]])],"derivedFrom":subQ3}),1.0]])]});}
            var Q1;
            {var subQ0=sQuery(id+"F3.wireOp",EDGE,"E33");var subQ1=sQuery(id+"F3.wireOp",EDGE,"E32");var subQ2=makeQuery(id+"F3.imprint","INTERSECT",VERTEX,{"derivedFrom":[sQuery(id+"F3.wireOp",EDGE,"E20"),subQ1,subQ0]});Q1=makeQuery(id+"F3.imprint","IMPRINT",FACE,{"disambiguationData":[TD([[makeQuery(id+"F3.imprint","IMPRINT",EDGE,{"disambiguationData":[TD([[subQ2,1.0]])],"derivedFrom":subQ1}),-1.0]])]});}
            var Q2;
            {var subQ1=sQuery(id+"F3.wireOp",EDGE,"E40");var subQ3=makeQuery(id+"F3.imprint","INTERSECT",VERTEX,{"derivedFrom":[subQ1,sQuery(id+"F3.wireOp",EDGE,"E49")]});Q2=makeQuery(id+"F3.imprint","IMPRINT",FACE,{"disambiguationData":[TD([[makeQuery(id+"F3.imprint","IMPRINT",EDGE,{"disambiguationData":[TD([[subQ3,-1.0]])],"derivedFrom":subQ1}),-1.0]])]});}
            var Q3;
            {var subQ1=sQuery(id+"F3.wireOp",EDGE,"E38");var subQ3=sQuery(id+"F3.wireOp",EDGE,"E56");var subQ4=makeQuery(id+"F3.imprint","INTERSECT",VERTEX,{"derivedFrom":[sQuery(id+"F3.wireOp",EDGE,"E34"),subQ1,subQ3]});Q3=makeQuery(id+"F3.imprint","IMPRINT",FACE,{"disambiguationData":[TD([[makeQuery(id+"F3.imprint","IMPRINT",EDGE,{"disambiguationData":[TD([[subQ4,-1.0]])],"derivedFrom":subQ3}),1.0]])]});}
            var Q4;
            {var subQ0=sQuery(id+"F3.wireOp",EDGE,"E37");var subQ1=sQuery(id+"F3.wireOp",EDGE,"E34");var subQ2=makeQuery(id+"F3.imprint","INTERSECT",VERTEX,{"derivedFrom":[sQuery(id+"F3.wireOp",EDGE,"E20"),subQ1,subQ0]});Q4=makeQuery(id+"F3.imprint","IMPRINT",FACE,{"disambiguationData":[TD([[makeQuery(id+"F3.imprint","IMPRINT",EDGE,{"disambiguationData":[TD([[subQ2,1.0]])],"derivedFrom":subQ1}),1.0]])]});}
            var Q5;
            {var subQ0=sQuery(id+"F3.wireOp",EDGE,"E46");var subQ1=sQuery(id+"F3.wireOp",EDGE,"E41");var subQ2=makeQuery(id+"F3.imprint","INTERSECT",VERTEX,{"derivedFrom":[subQ1,subQ0]});Q5=makeQuery(id+"F3.imprint","IMPRINT",FACE,{"disambiguationData":[TD([[makeQuery(id+"F3.imprint","IMPRINT",EDGE,{"disambiguationData":[TD([[subQ2,1.0]])],"derivedFrom":subQ0}),1.0]])]});}
            var Q6;
            {var subQ3=sQuery(id+"F3.wireOp",EDGE,"E56");var subQ5=sQuery(id+"F3.wireOp",EDGE,"E41");var subQ6=makeQuery(id+"F3.imprint","INTERSECT",VERTEX,{"derivedFrom":[subQ5,subQ3]});Q6=makeQuery(id+"F3.imprint","IMPRINT",FACE,{"disambiguationData":[TD([[makeQuery(id+"F3.imprint","IMPRINT",EDGE,{"disambiguationData":[TD([[subQ6,-1.0]])],"derivedFrom":subQ5}),-1.0]])]});}
            extrude(context, id + "F16", {"entities" : qUnion([Q0, Q1, Q2, Q3, Q4, Q5, Q6]), "depth" : 3 * mm});
        }
        {
            var Q0;
            Q0=makeQuery(id+"F16.opExtrude","CAP_FACE",FACE,{"disambiguationData":[OSD([sQuery(id+"F3.wireOp",EDGE,"E30"),sQuery(id+"F3.wireOp",EDGE,"E31"),sQuery(id+"F3.wireOp",EDGE,"E56")])],"isStart":false});
            var Q1;
            Q1=makeQuery(id+"F16.opExtrude","CAP_FACE",FACE,{"disambiguationData":[OSD([sQuery(id+"F3.wireOp",EDGE,"E32"),sQuery(id+"F3.wireOp",EDGE,"E33"),sQuery(id+"F3.wireOp",EDGE,"E56")])],"isStart":false});
            var Q2;
            Q2=makeQuery(id+"F13.opExtrude","CAP_FACE",FACE,{"disambiguationData":[OSD([sQuery(id+"F3.wireOp",EDGE,"E33"),sQuery(id+"F3.wireOp",EDGE,"E38"),sQuery(id+"F3.wireOp",EDGE,"E56")])],"isStart":false});
            var Q3;
            Q3=makeQuery(id+"F13.opExtrude","CAP_FACE",FACE,{"disambiguationData":[OSD([sQuery(id+"F3.wireOp",EDGE,"E34"),sQuery(id+"F3.wireOp",EDGE,"E43"),sQuery(id+"F3.wireOp",EDGE,"E56")])],"isStart":false});
            var Q4;
            Q4=makeQuery(id+"F13.opExtrude","CAP_FACE",FACE,{"disambiguationData":[OSD([sQuery(id+"F3.wireOp",EDGE,"E40"),sQuery(id+"F3.wireOp",EDGE,"E42"),sQuery(id+"F3.wireOp",EDGE,"E44"),sQuery(id+"F3.wireOp",EDGE,"E56")])],"isStart":false});
            var Q5;
            Q5=makeQuery(id+"F16.opExtrude","CAP_FACE",FACE,{"disambiguationData":[OSD([sQuery(id+"F3.wireOp",EDGE,"E40"),sQuery(id+"F3.wireOp",EDGE,"E43"),sQuery(id+"F3.wireOp",EDGE,"E56")])],"isStart":false});
            var Q6;
            Q6=makeQuery(id+"F16.opExtrude","CAP_FACE",FACE,{"disambiguationData":[OSD([sQuery(id+"F3.wireOp",EDGE,"E38"),sQuery(id+"F3.wireOp",EDGE,"E42"),sQuery(id+"F3.wireOp",EDGE,"E56")])],"isStart":false});
            chamfer(context, id + "F17", {"entities" : qUnion([Q0, Q1, Q2, Q3, Q4, Q5, Q6]), "chamferType" : ChamferType.OFFSET_ANGLE, "width" : 3 * mm, "oppositeDirection" : false, "angle" : 59 * degree, "tangentPropagation" : true});
        }
        {
            var Q0;
            Q0=makeQuery(id+"F16.opExtrude","CAP_FACE",FACE,{"disambiguationData":[OSD([sQuery(id+"F3.wireOp",EDGE,"E34"),sQuery(id+"F3.wireOp",EDGE,"E37"),sQuery(id+"F3.wireOp",EDGE,"E56")])],"isStart":false});
            var Q1;
            Q1=makeQuery(id+"F16.opExtrude","CAP_FACE",FACE,{"disambiguationData":[OSD([sQuery(id+"F3.wireOp",EDGE,"E41"),sQuery(id+"F3.wireOp",EDGE,"E44"),sQuery(id+"F3.wireOp",EDGE,"E46"),sQuery(id+"F3.wireOp",EDGE,"E56")])],"isStart":false});
            chamfer(context, id + "F18", {"entities" : qUnion([Q0, Q1]), "chamferType" : ChamferType.OFFSET_ANGLE, "width" : 3 * mm, "oppositeDirection" : true, "angle" : 59 * degree, "tangentPropagation" : true});
        }
        {
            var Q0;
            {var subQ0=sQuery(id+"F3.wireOp",EDGE,"E44");Q0=makeQuery(id+"F13.opExtrude","CAP_EDGE",EDGE,{"disambiguationData":[OSD([subQ0]),TDD([makeQuery(id+"F3.imprint","IMPRINT",EDGE,{"disambiguationData":[TD([[makeQuery(id+"F3.imprint","INTERSECT",VERTEX,{"derivedFrom":[sQuery(id+"F3.wireOp",EDGE,"E12"),subQ0]}),1.0]])],"derivedFrom":subQ0})])],"isStart":false});}
            var Q1;
            {var subQ0=sQuery(id+"F3.wireOp",EDGE,"E48");Q1=makeQuery(id+"F4.opExtrude","CAP_EDGE",EDGE,{"disambiguationData":[OSD([subQ0]),TDD([makeQuery(id+"F3.imprint","IMPRINT",EDGE,{"disambiguationData":[TD([[makeQuery(id+"F3.imprint","INTERSECT",VERTEX,{"derivedFrom":[subQ0,sQuery(id+"F3.wireOp",EDGE,"E54")]}),1.0]])],"derivedFrom":subQ0})])],"isStart":false});}
            var Q2;
            {var subQ0=sQuery(id+"F3.wireOp",EDGE,"E52");Q2=makeQuery(id+"F4.opExtrude","CAP_EDGE",EDGE,{"disambiguationData":[OSD([subQ0]),TDD([makeQuery(id+"F3.imprint","IMPRINT",EDGE,{"disambiguationData":[TD([[makeQuery(id+"F3.imprint","INTERSECT",VERTEX,{"derivedFrom":[subQ0,sQuery(id+"F3.wireOp",EDGE,"E58")]}),1.0]])],"derivedFrom":subQ0})])],"isStart":false});}
            chamfer(context, id + "F19", {"entities" : qUnion([Q0, Q1, Q2]), "chamferType" : ChamferType.OFFSET_ANGLE, "width" : 8 * mm, "oppositeDirection" : true, "angle" : 20 * degree, "tangentPropagation" : true});
        }
        {
            var Q0;
            {var subQ0=sQuery(id+"F3.wireOp",EDGE,"E50");Q0=makeQuery(id+"F13.opExtrude","CAP_EDGE",EDGE,{"disambiguationData":[OSD([subQ0]),TDD([makeQuery(id+"F3.imprint","IMPRINT",EDGE,{"disambiguationData":[TD([[makeQuery(id+"F3.imprint","INTERSECT",VERTEX,{"derivedFrom":[subQ0,sQuery(id+"F3.wireOp",EDGE,"E52")]}),1.0]])],"derivedFrom":subQ0})])],"isStart":false});}
            var Q1;
            {var subQ0=sQuery(id+"F3.wireOp",EDGE,"E46");Q1=makeQuery(id+"F13.opExtrude","CAP_EDGE",EDGE,{"disambiguationData":[OSD([subQ0]),TDD([makeQuery(id+"F3.imprint","IMPRINT",EDGE,{"disambiguationData":[TD([[makeQuery(id+"F3.imprint","INTERSECT",VERTEX,{"derivedFrom":[sQuery(id+"F3.wireOp",EDGE,"E41"),subQ0]}),-1.0]])],"derivedFrom":subQ0})])],"isStart":false});}
            chamfer(context, id + "F20", {"entities" : qUnion([Q0, Q1]), "chamferType" : ChamferType.OFFSET_ANGLE, "width" : 8 * mm, "oppositeDirection" : false, "angle" : 20 * degree, "tangentPropagation" : true});
        }
        {
            var Q0;
            {var subQ0=sQuery(id+"F3.wireOp",EDGE,"E41");Q0=makeQuery(id+"F13.opExtrude","CAP_EDGE",EDGE,{"disambiguationData":[OSD([subQ0]),TDD([makeQuery(id+"F3.imprint","IMPRINT",EDGE,{"disambiguationData":[TD([[makeQuery(id+"F3.imprint","INTERSECT",VERTEX,{"derivedFrom":[subQ0,sQuery(id+"F3.wireOp",EDGE,"E56")]}),1.0]])],"derivedFrom":subQ0})])],"isStart":false});}
            var Q1;
            {var subQ0=sQuery(id+"F3.wireOp",EDGE,"E46");Q1=makeQuery(id+"F16.opExtrude","CAP_EDGE",EDGE,{"disambiguationData":[OSD([subQ0]),TDD([makeQuery(id+"F3.imprint","IMPRINT",EDGE,{"disambiguationData":[TD([[makeQuery(id+"F3.imprint","INTERSECT",VERTEX,{"derivedFrom":[sQuery(id+"F3.wireOp",EDGE,"E41"),subQ0]}),-1.0]])],"derivedFrom":subQ0})])],"isStart":false});}
            chamfer(context, id + "F21", {"entities" : qUnion([Q0, Q1]), "chamferType" : ChamferType.OFFSET_ANGLE, "width" : 8 * mm, "oppositeDirection" : true, "angle" : 20 * degree, "tangentPropagation" : true});
        }
    });
